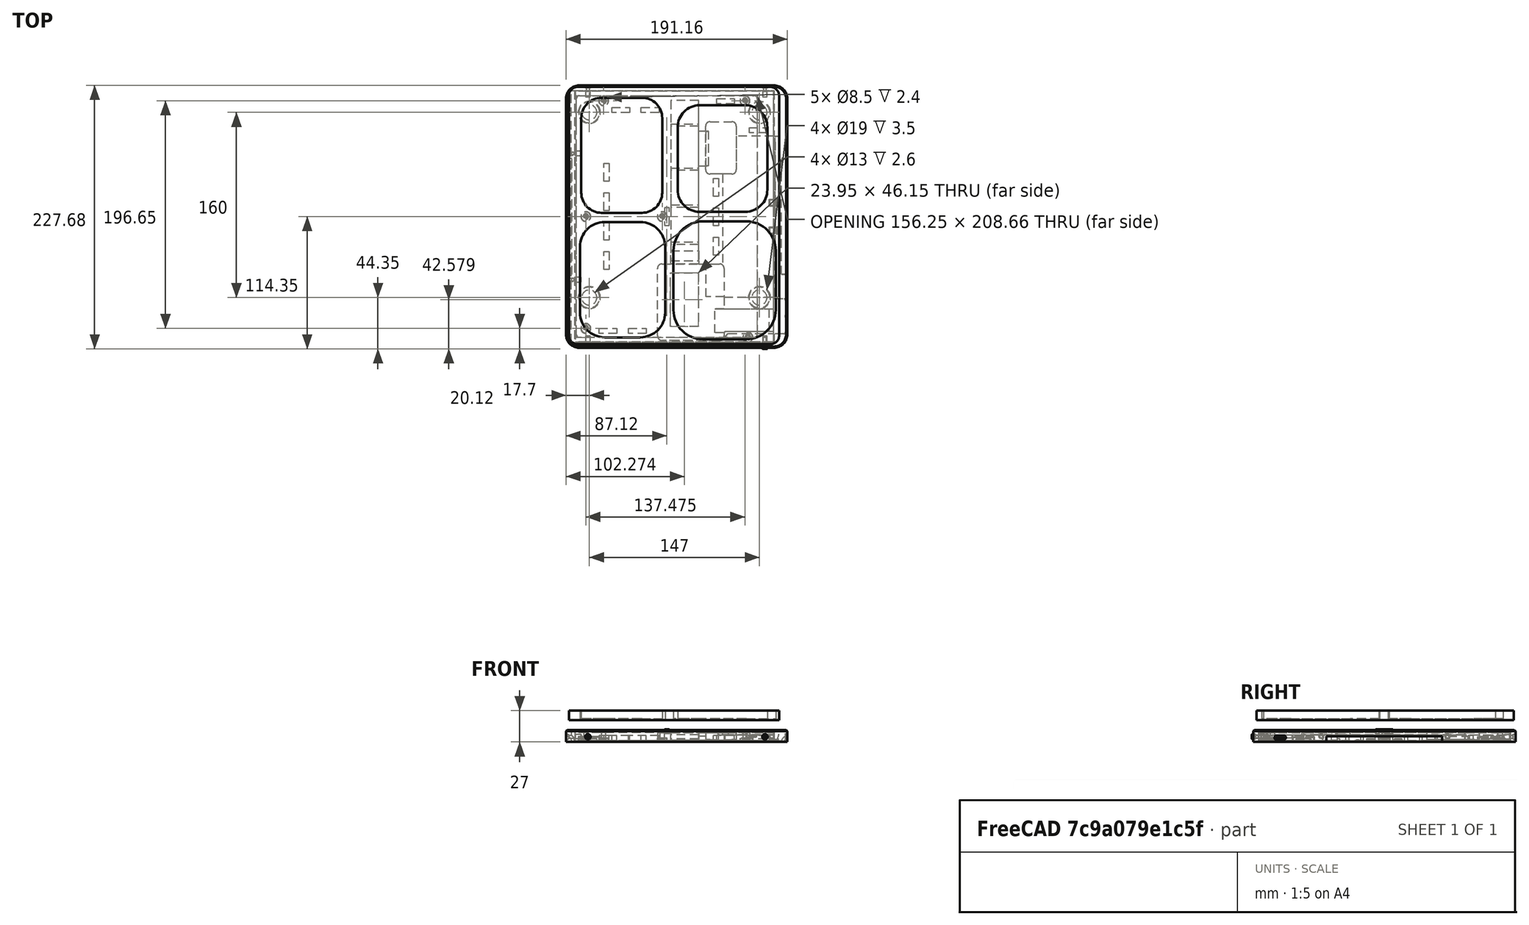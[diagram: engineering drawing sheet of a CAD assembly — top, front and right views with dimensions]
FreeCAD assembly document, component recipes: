
FREECAD ASSEMBLY — COMPONENT RECIPES ("freezer-display-assembly")

This assembly document has 5 components, labeled P0..P4 below (a component is one placed body or linked part). 5 of them carry a construction recipe — the FreeCAD feature program that regenerates the part from scratch, quoted from this document or its linked companion documents; the rest are supplied as boundary geometry only. No exploded tour is included for this assembly.
COMPONENT P0 — recipe-attached ("placeholder", modeled in this document).
Construction recipe (the document's own serialized feature program — sketch geometry with constraints, then the solid features built on it; lengths are millimeters unless a unit is written):

FEATURE [Sketcher::SketchObject] Sketch004
  AttachmentOffset = pos=(0,0,10) rot=(0,0,1;0rad)
  AttachmentSupport = -> [XY_Plane003]
  FullyConstrained = false
  MapMode = 5
  Placement = pos=(0,0,10) rot=(0,0,1;0rad)
  sketch-geometry (10):
    g0: ArcOfCircle CenterX=-77.1526 CenterY=104.437 CenterZ=0 NormalX=0 NormalY=0 NormalZ=1 AngleXU=0 Radius=7.5 StartAngle=1.5708 EndAngle=3.14159
    g1: LineSegment StartX=-77.1526 StartY=111.937 StartZ=0 EndX=89.4898 EndY=111.937 EndZ=0
    g2: ArcOfCircle CenterX=89.4898 CenterY=104.437 CenterZ=0 NormalX=0 NormalY=0 NormalZ=1 AngleXU=0 Radius=7.5 StartAngle=0 EndAngle=1.5708
    g3: LineSegment StartX=96.9898 StartY=104.437 StartZ=0 EndX=96.9898 EndY=-102.808 EndZ=0
    g4: ArcOfCircle CenterX=89.4898 CenterY=-102.808 CenterZ=0 NormalX=0 NormalY=0 NormalZ=1 AngleXU=0 Radius=7.5 StartAngle=4.71239 EndAngle=6.28319
    g5: LineSegment StartX=89.4898 StartY=-110.308 StartZ=0 EndX=-77.1526 EndY=-110.308 EndZ=0
    g6: ArcOfCircle CenterX=-77.1526 CenterY=-102.808 CenterZ=0 NormalX=0 NormalY=0 NormalZ=1 AngleXU=0 Radius=7.5 StartAngle=3.14159 EndAngle=4.71239
    g7: LineSegment StartX=-84.6526 StartY=-102.808 StartZ=0 EndX=-84.6526 EndY=104.437 EndZ=0
    g8: GeomPoint X=-84.6526 Y=111.937 Z=0
    g9: GeomPoint X=96.9898 Y=-110.308 Z=0
  constraints (20):
    c: Tangent(g0,g1) = 1.5708
    c: Tangent(g1,g2) = 1.5708
    c: Tangent(g2,g3) = 1.5708
    c: Tangent(g3,g4) = 1.5708
    c: Tangent(g4,g5) = 1.5708
    c: Tangent(g5,g6) = 1.5708
    c: Tangent(g6,g7) = 1.5708
    c: Tangent(g7,g0) = 1.5708
    c: Horizontal(g1)
    c: Horizontal(g5)
    c: Vertical(g3)
    c: Vertical(g7)
    c: Equal(g0,g2)
    c: Equal(g2,g4)
    c: Equal(g4,g6)
    c: PointOnObject(g8,g1)
    c: PointOnObject(g8,g7)
    c: PointOnObject(g9,g3)
    c: PointOnObject(g9,g5)
    c: Diameter(g4) = 15
FEATURE [PartDesign::Pad] Pad003
  Direction = (0,0,1)
  Length = 8
  Length2 = 10
  Profile = -> Sketch004
  ReferenceAxis = -> Sketch004 [N_Axis]
  Refine = true
  Suppressed = false
  Type = 0
FEATURE [Sketcher::SketchObject] Sketch005
  AttachmentSupport = -> [Pad003]
  FullyConstrained = false
  MapMode = 5
  Placement = pos=(0,0,18) rot=(0,0,1;0rad)
  sketch-geometry (40):
    g0: ArcOfCircle CenterX=-56.4829 CenterY=85.1627 CenterZ=0 NormalX=0 NormalY=0 NormalZ=1 AngleXU=0 Radius=17.496 StartAngle=1.5708 EndAngle=3.14159
    g1: LineSegment StartX=-56.4829 StartY=102.659 StartZ=0 EndX=-21.4911 EndY=102.659 EndZ=0
    g2: ArcOfCircle CenterX=-21.4911 CenterY=85.1627 CenterZ=0 NormalX=0 NormalY=0 NormalZ=1 AngleXU=0 Radius=17.496 StartAngle=1e-16 EndAngle=1.5708
    g3: LineSegment StartX=-3.99511 StartY=85.1627 StartZ=0 EndX=-3.99511 EndY=20.7193 EndZ=0
    g4: ArcOfCircle CenterX=-21.4911 CenterY=20.7193 CenterZ=0 NormalX=0 NormalY=0 NormalZ=1 AngleXU=0 Radius=17.496 StartAngle=4.71239 EndAngle=6.28319
    g5: LineSegment StartX=-21.4911 StartY=3.22331 StartZ=0 EndX=-56.4829 EndY=3.22331 EndZ=0
    g6: ArcOfCircle CenterX=-56.4829 CenterY=20.7193 CenterZ=0 NormalX=0 NormalY=0 NormalZ=1 AngleXU=0 Radius=17.496 StartAngle=3.14159 EndAngle=4.71239
    g7: LineSegment StartX=-73.9789 StartY=20.7193 StartZ=0 EndX=-73.9789 EndY=85.1627 EndZ=0
    g8: GeomPoint X=-73.9789 Y=102.659 Z=0
    g9: GeomPoint X=-3.99511 Y=3.22331 Z=0
    g10: ArcOfCircle CenterX=28.3724 CenterY=77.0631 CenterZ=0 NormalX=0 NormalY=0 NormalZ=1 AngleXU=0 Radius=19.05 StartAngle=1.5708 EndAngle=3.14159
    g11: LineSegment StartX=28.3724 StartY=96.1131 StartZ=0 EndX=67.8034 EndY=96.1131 EndZ=0
    g12: ArcOfCircle CenterX=67.8034 CenterY=77.0631 CenterZ=0 NormalX=0 NormalY=0 NormalZ=1 AngleXU=0 Radius=19.05 StartAngle=1e-16 EndAngle=1.5708
    g13: LineSegment StartX=86.8535 StartY=77.0631 StartZ=0 EndX=86.8535 EndY=23.1482 EndZ=0
    g14: ArcOfCircle CenterX=67.8034 CenterY=23.1482 CenterZ=0 NormalX=0 NormalY=0 NormalZ=1 AngleXU=0 Radius=19.05 StartAngle=4.71239 EndAngle=6.28319
    g15: LineSegment StartX=67.8034 StartY=4.09812 StartZ=0 EndX=28.3724 EndY=4.09812 EndZ=0
    g16: ArcOfCircle CenterX=28.3724 CenterY=23.1482 CenterZ=0 NormalX=0 NormalY=0 NormalZ=1 AngleXU=0 Radius=19.05 StartAngle=3.14159 EndAngle=4.71239
    g17: LineSegment StartX=9.32233 StartY=23.1482 StartZ=0 EndX=9.32233 EndY=77.0631 EndZ=0
    g18: GeomPoint X=9.32233 Y=96.1131 Z=0
    g19: GeomPoint X=86.8535 Y=4.09812 Z=0
    g20: ArcOfCircle CenterX=-53.6616 CenterY=-26.1553 CenterZ=0 NormalX=0 NormalY=0 NormalZ=1 AngleXU=0 Radius=21.4402 StartAngle=1.5708 EndAngle=3.14159
    g21: LineSegment StartX=-53.6616 StartY=-4.71507 StartZ=0 EndX=-22.8762 EndY=-4.71507 EndZ=0
    g22: ArcOfCircle CenterX=-22.8762 CenterY=-26.1553 CenterZ=0 NormalX=0 NormalY=0 NormalZ=1 AngleXU=0 Radius=21.4402 StartAngle=1e-16 EndAngle=1.5708
    g23: LineSegment StartX=-1.43594 StartY=-26.1553 StartZ=0 EndX=-1.43594 EndY=-82.893 EndZ=0
    g24: ArcOfCircle CenterX=-22.8762 CenterY=-82.893 CenterZ=0 NormalX=0 NormalY=0 NormalZ=1 AngleXU=0 Radius=21.4402 StartAngle=4.71239 EndAngle=6.28319
    g25: LineSegment StartX=-22.8762 StartY=-104.333 StartZ=0 EndX=-53.6616 EndY=-104.333 EndZ=0
    g26: ArcOfCircle CenterX=-53.6616 CenterY=-82.893 CenterZ=0 NormalX=0 NormalY=0 NormalZ=1 AngleXU=0 Radius=21.4402 StartAngle=3.14159 EndAngle=4.71239
    g27: LineSegment StartX=-75.1018 StartY=-82.893 StartZ=0 EndX=-75.1018 EndY=-26.1553 EndZ=0
    g28: GeomPoint X=-75.1018 Y=-4.71507 Z=0
    g29: GeomPoint X=-1.43594 Y=-104.333 Z=0
    g30: ArcOfCircle CenterX=30.9968 CenterY=-29.4358 CenterZ=0 NormalX=0 NormalY=0 NormalZ=1 AngleXU=0 Radius=25.2768 StartAngle=1.5708 EndAngle=3.14159
    g31: LineSegment StartX=30.9968 StartY=-4.15898 StartZ=0 EndX=68.8382 EndY=-4.15898 EndZ=0
    g32: ArcOfCircle CenterX=68.8382 CenterY=-29.4358 CenterZ=0 NormalX=0 NormalY=0 NormalZ=1 AngleXU=0 Radius=25.2768 StartAngle=2e-16 EndAngle=1.5708
    g33: LineSegment StartX=94.115 StartY=-29.4358 StartZ=0 EndX=94.115 EndY=-80.6908 EndZ=0
    g34: ArcOfCircle CenterX=68.8382 CenterY=-80.6908 CenterZ=0 NormalX=0 NormalY=0 NormalZ=1 AngleXU=0 Radius=25.2768 StartAngle=4.71239 EndAngle=6.28319
    g35: LineSegment StartX=68.8382 StartY=-105.968 StartZ=0 EndX=30.9968 EndY=-105.968 EndZ=0
    g36: ArcOfCircle CenterX=30.9968 CenterY=-80.6908 CenterZ=0 NormalX=0 NormalY=0 NormalZ=1 AngleXU=0 Radius=25.2768 StartAngle=3.14159 EndAngle=4.71239
    g37: LineSegment StartX=5.71998 StartY=-80.6908 StartZ=0 EndX=5.71998 EndY=-29.4358 EndZ=0
    g38: GeomPoint X=5.71998 Y=-4.15898 Z=0
    g39: GeomPoint X=94.115 Y=-105.968 Z=0
  constraints (76):
    c: Tangent(g0,g1) = 1.5708
    c: Tangent(g1,g2) = 1.5708
    c: Tangent(g2,g3) = 1.5708
    c: Tangent(g3,g4) = 1.5708
    c: Tangent(g4,g5) = 1.5708
    c: Tangent(g5,g6) = 1.5708
    c: Tangent(g6,g7) = 1.5708
    c: Tangent(g7,g0) = 1.5708
    c: Horizontal(g1)
    c: Horizontal(g5)
    c: Vertical(g3)
    c: Vertical(g7)
    c: Equal(g0,g2)
    c: Equal(g2,g4)
    c: Equal(g4,g6)
    c: PointOnObject(g8,g1)
    c: PointOnObject(g8,g7)
    c: PointOnObject(g9,g3)
    c: PointOnObject(g9,g5)
    c: Tangent(g10,g11) = 1.5708
    c: Tangent(g11,g12) = 1.5708
    c: Tangent(g12,g13) = 1.5708
    c: Tangent(g13,g14) = 1.5708
    c: Tangent(g14,g15) = 1.5708
    c: Tangent(g15,g16) = 1.5708
    c: Tangent(g16,g17) = 1.5708
    c: Tangent(g17,g10) = 1.5708
    c: Horizontal(g11)
    c: Horizontal(g15)
    c: Vertical(g13)
    c: Vertical(g17)
    c: Equal(g10,g12)
    c: Equal(g12,g14)
    c: Equal(g14,g16)
    c: PointOnObject(g18,g11)
    c: PointOnObject(g18,g17)
    c: PointOnObject(g19,g13)
    c: PointOnObject(g19,g15)
    c: Tangent(g20,g21) = 1.5708
    c: Tangent(g21,g22) = 1.5708
    c: Tangent(g22,g23) = 1.5708
    c: Tangent(g23,g24) = 1.5708
    c: Tangent(g24,g25) = 1.5708
    c: Tangent(g25,g26) = 1.5708
    c: Tangent(g26,g27) = 1.5708
    c: Tangent(g27,g20) = 1.5708
    c: Horizontal(g21)
    c: Horizontal(g25)
    c: Vertical(g23)
    c: Vertical(g27)
    c: Equal(g20,g22)
    c: Equal(g22,g24)
    c: Equal(g24,g26)
    c: PointOnObject(g28,g21)
    c: PointOnObject(g28,g27)
    c: PointOnObject(g29,g23)
    c: PointOnObject(g29,g25)
    c: Tangent(g30,g31) = 1.5708
    c: Tangent(g31,g32) = 1.5708
    c: Tangent(g32,g33) = 1.5708
    c: Tangent(g33,g34) = 1.5708
    c: Tangent(g34,g35) = 1.5708
    c: Tangent(g35,g36) = 1.5708
    c: Tangent(g36,g37) = 1.5708
    c: Tangent(g37,g30) = 1.5708
    c: Horizontal(g31)
    c: Horizontal(g35)
    c: Vertical(g33)
    c: Vertical(g37)
    c: Equal(g30,g32)
    c: Equal(g32,g34)
    c: Equal(g34,g36)
    c: PointOnObject(g38,g31)
    c: PointOnObject(g38,g37)
    c: PointOnObject(g39,g33)
    c: PointOnObject(g39,g35)
FEATURE [PartDesign::Pocket] Pocket
  BaseFeature = -> Pad003
  Direction = (0,0,-1)
  Length = 7
  Length2 = 5
  Profile = -> Sketch005
  ReferenceAxis = -> Sketch005 [N_Axis]
  Refine = true
  Suppressed = false
  Type = 0
FEATURE [PartDesign::Body] Body  label="placeholder"
  Group = -> [Sketch004,Pad003,Sketch005,Pocket]
  Origin = -> Origin003
  Tip = -> Pocket
COMPONENT P1 — recipe-attached ("SLS-frame", modeled in this document).
Construction recipe (the document's own serialized feature program — sketch geometry with constraints, then the solid features built on it; lengths are millimeters unless a unit is written):

FEATURE [Sketcher::SketchObject] Sketch006
  AttachmentSupport = -> [XY_Plane004]
  FullyConstrained = false
  MapMode = 5
  sketch-geometry (21):
    g0: ArcOfCircle CenterX=-75.625 CenterY=101.83 CenterZ=0 NormalX=0 NormalY=0 NormalZ=1 AngleXU=0 Radius=2.5 StartAngle=1.5708 EndAngle=3.14159
    g1: LineSegment StartX=-75.625 StartY=104.33 StartZ=0 EndX=75.625 EndY=104.33 EndZ=0
    g2: ArcOfCircle CenterX=75.625 CenterY=101.83 CenterZ=0 NormalX=0 NormalY=0 NormalZ=1 AngleXU=0 Radius=2.5 StartAngle=8e-16 EndAngle=1.5708
    g3: LineSegment StartX=78.125 StartY=101.83 StartZ=0 EndX=78.125 EndY=-101.83 EndZ=0
    g4: ArcOfCircle CenterX=75.625 CenterY=-101.83 CenterZ=0 NormalX=0 NormalY=0 NormalZ=1 AngleXU=0 Radius=2.5 StartAngle=4.71239 EndAngle=6.28319
    g5: LineSegment StartX=75.625 StartY=-104.33 StartZ=0 EndX=-75.625 EndY=-104.33 EndZ=0
    g6: ArcOfCircle CenterX=-75.625 CenterY=-101.83 CenterZ=0 NormalX=0 NormalY=0 NormalZ=1 AngleXU=0 Radius=2.5 StartAngle=3.14159 EndAngle=4.71239
    g7: LineSegment StartX=-78.125 StartY=-101.83 StartZ=0 EndX=-78.125 EndY=101.83 EndZ=0
    g8: GeomPoint X=-78.125 Y=104.33 Z=0
    g9: GeomPoint X=78.125 Y=-104.33 Z=0
    g10: ArcOfCircle CenterX=-75.625 CenterY=101.83 CenterZ=0 NormalX=0 NormalY=0 NormalZ=1 AngleXU=0 Radius=11.5 StartAngle=1.5708 EndAngle=3.14159
    g11: LineSegment StartX=-75.625 StartY=113.33 StartZ=0 EndX=92.5389 EndY=113.33 EndZ=0
    g12: ArcOfCircle CenterX=92.5389 CenterY=101.83 CenterZ=0 NormalX=0 NormalY=0 NormalZ=1 AngleXU=0 Radius=11.5 StartAngle=7e-16 EndAngle=1.5708
    g13: LineSegment StartX=104.039 StartY=101.83 StartZ=0 EndX=104.039 EndY=-101.83 EndZ=0
    g14: ArcOfCircle CenterX=92.5389 CenterY=-101.83 CenterZ=0 NormalX=0 NormalY=0 NormalZ=1 AngleXU=0 Radius=11.5 StartAngle=4.71239 EndAngle=6.28319
    g15: LineSegment StartX=92.5389 StartY=-113.33 StartZ=0 EndX=-75.625 EndY=-113.33 EndZ=0
    g16: ArcOfCircle CenterX=-75.625 CenterY=-101.83 CenterZ=0 NormalX=0 NormalY=0 NormalZ=1 AngleXU=0 Radius=11.5 StartAngle=3.14159 EndAngle=4.71239
    g17: LineSegment StartX=-87.125 StartY=-101.83 StartZ=0 EndX=-87.125 EndY=101.83 EndZ=0
    g18: GeomPoint X=-87.125 Y=113.33 Z=0
    g19: GeomPoint X=104.039 Y=-113.33 Z=0
    g20: LineSegment StartX=-83.7787 StartY=109.94 StartZ=0 EndX=-82.1303 EndY=108.314 EndZ=0
  constraints (45):
    c: Tangent(g0,g1) = 1.5708
    c: Tangent(g1,g2) = 1.5708
    c: Tangent(g2,g3) = 1.5708
    c: Tangent(g3,g4) = 1.5708
    c: Tangent(g4,g5) = 1.5708
    c: Tangent(g5,g6) = 1.5708
    c: Tangent(g6,g7) = 1.5708
    c: Tangent(g7,g0) = 1.5708
    c: Horizontal(g1)
    c: Horizontal(g5)
    c: Vertical(g3)
    c: Vertical(g7)
    c: Equal(g0,g2)
    c: Equal(g2,g4)
    c: PointOnObject(g8,g1)
    c: PointOnObject(g8,g7)
    c: PointOnObject(g9,g3)
    c: PointOnObject(g9,g5)
    c: Diameter(g4) = 5
    c: DistanceX(g0,g2) = 156.25
    c: Symmetric(g0,g4,g-1)
    c: DistanceY(g5,g0) = 208.66
    c: Tangent(g10,g11) = 1.5708
    c: Tangent(g11,g12) = 1.5708
    c: Tangent(g12,g13) = 1.5708
    c: Tangent(g13,g14) = 1.5708
    c: Tangent(g14,g15) = 1.5708
    c: Tangent(g15,g16) = 1.5708
    c: Tangent(g16,g17) = 1.5708
    c: Tangent(g17,g10) = 1.5708
    c: Horizontal(g11)
    c: Horizontal(g15)
    c: Vertical(g13)
    c: Equal(g10,g12)
    c: Equal(g12,g14)
    c: PointOnObject(g18,g11)
    c: PointOnObject(g18,g17)
    c: PointOnObject(g19,g13)
    c: PointOnObject(g19,g15)
    c: Diameter(g10) = 23
    c: Coincident(g10,g0)
    c: Symmetric(g10,g16,g-1)
    c: Coincident(g16,g6)
    c: PointOnObject(g20,g10)
    c: Distance(g20) = 2.31538
FEATURE [PartDesign::Pad] Pad004  label="front-opening-bulk-shape"
  Direction = (0,0,1)
  Length = 1.2
  Length2 = 9
  Profile = -> Sketch006
  ReferenceAxis = -> Sketch006 [N_Axis]
  Refine = true
  Suppressed = false
  Type = 4
FEATURE [Sketcher::SketchObject] Sketch007
  AttachmentSupport = -> [XY_Plane004]
  FullyConstrained = false
  MapMode = 5
  Placement = pos=(0,0,0) rot=(0,1,0;3.14159rad)
  expr: Constraints[8] = 174.4 + 1
  expr: Constraints[9] = 216.7 + 1
  sketch-geometry (4):
    g0: LineSegment StartX=82.6332 StartY=108.85 StartZ=0 EndX=-92.7668 EndY=108.85 EndZ=0
    g1: LineSegment StartX=-92.7668 StartY=108.85 StartZ=0 EndX=-92.7668 EndY=-108.85 EndZ=0
    g2: LineSegment StartX=-92.7668 StartY=-108.85 StartZ=0 EndX=82.6332 EndY=-108.85 EndZ=0
    g3: LineSegment StartX=82.6332 StartY=-108.85 StartZ=0 EndX=82.6332 EndY=108.85 EndZ=0
  constraints (10):
    c: Coincident(g0,g1)
    c: Coincident(g1,g2)
    c: Coincident(g2,g3)
    c: Coincident(g3,g0)
    c: Horizontal(g0)
    c: Horizontal(g2)
    c: Vertical(g1)
    c: Symmetric(g0,g2,g-1)
    c: DistanceX(g0,g0) = 175.4
    c: DistanceY(g3,g3) = 217.7
FEATURE [PartDesign::Pocket] Pocket001  label="dispaly-insertion-point"
  BaseFeature = -> Pad004
  Direction = (0,0,1)
  Length = 19
  Length2 = 5
  Profile = -> Sketch007
  ReferenceAxis = -> Sketch007 [N_Axis]
  Refine = true
  Reversed = true
  Suppressed = false
  Type = 0
FEATURE [Sketcher::SketchObject] Sketch008
  AttachmentSupport = -> [XZ_Plane004]
  ExternalGeometry = -> [Sketch006]
  FullyConstrained = false
  MapMode = 5
  Placement = pos=(0,0,0) rot=(1,0,0;1.5708rad)
  sketch-geometry (6):
    g0: Circle CenterX=-87.125 CenterY=-9 CenterZ=0 NormalX=0 NormalY=0 NormalZ=1 AngleXU=0 Radius=7.5
    g1: LineSegment StartX=-87.125 StartY=-9 StartZ=0 EndX=-87.125 EndY=0 EndZ=0
    g2: ArcOfCircle CenterX=-87.125 CenterY=-9 CenterZ=0 NormalX=0 NormalY=0 NormalZ=1 AngleXU=0 Radius=7.5 StartAngle=0 EndAngle=1.04963
    g3: LineSegment StartX=-87.125 StartY=-9 StartZ=0 EndX=-61.4654 EndY=-9 EndZ=0
    g4: LineSegment StartX=-79.625 StartY=-9 StartZ=0 EndX=-83.3908 EndY=-9 EndZ=0
    g5: LineSegment StartX=-83.3908 StartY=-2.49572 StartZ=0 EndX=-83.3908 EndY=-9 EndZ=0
  constraints (15):
    c: DistanceY(g0,g-1) = 9
    c: Diameter(g0) = 15
    c: Coincident(g1,g0)
    c: Coincident(g1,g-3)
    c: Vertical(g1)
    c: Coincident(g2,g0)
    c: PointOnObject(g2,g0)
    c: Coincident(g3,g2)
    c: Horizontal(g3)
    c: PointOnObject(g2,g3)
    c: Coincident(g4,g2)
    c: Vertical(g5)
    c: Coincident(g2,g5)
    c: Coincident(g4,g5)
    c: Horizontal(g4)
FEATURE [PartDesign::Pad] Pad005  label="handle-bulk"
  BaseFeature = -> Pocket001
  Direction = (0,-1,2e-16)
  Length = 220
  Length2 = 10
  Midplane = true
  Profile = -> Sketch008
  ReferenceAxis = -> Sketch008 [N_Axis]
  Refine = true
  Suppressed = false
  Type = 0
FEATURE [Sketcher::SketchObject] Sketch009
  AttachmentSupport = -> [XZ_Plane004]
  ExternalGeometry = -> [Sketch008,Sketch006]
  FullyConstrained = true
  MapMode = 5
  Placement = pos=(0,0,0) rot=(1,0,0;1.5708rad)
  sketch-geometry (8):
    g0: ArcOfCircle CenterX=-87.125 CenterY=-9 CenterZ=0 NormalX=0 NormalY=0 NormalZ=1 AngleXU=0 Radius=5 StartAngle=0 EndAngle=1.5708
    g1: LineSegment StartX=-82.125 StartY=-9 StartZ=0 EndX=-87.125 EndY=-9 EndZ=0
    g2: LineSegment StartX=-87.125 StartY=-9 StartZ=0 EndX=-87.125 EndY=-4 EndZ=0
    g3: LineSegment StartX=-79.625 StartY=-9 StartZ=0 EndX=104.039 EndY=-9 EndZ=0
    g4: ArcOfCircle CenterX=104.039 CenterY=-9 CenterZ=0 NormalX=0 NormalY=0 NormalZ=1 AngleXU=0 Radius=5 StartAngle=1.5708 EndAngle=3.14159
    g5: LineSegment StartX=104.039 StartY=-9 StartZ=0 EndX=104.039 EndY=0 EndZ=0
    g6: LineSegment StartX=99.0389 StartY=-9 StartZ=0 EndX=104.039 EndY=-9 EndZ=0
    g7: LineSegment StartX=104.039 StartY=-9 StartZ=0 EndX=104.039 EndY=-4 EndZ=0
  constraints (22):
    c: Coincident(g0,g-3)
    c: Coincident(g1,g0)
    c: Coincident(g1,g0)
    c: Horizontal(g1)
    c: Coincident(g2,g0)
    c: Coincident(g2,g0)
    c: Vertical(g2)
    c: DistanceX(g0,g-3) = 2.5
    c: DistanceY(g0,g0) = 5
    c: Coincident(g3,g-3)
    c: Horizontal(g3)
    c: Coincident(g4,g3)
    c: PointOnObject(g4,g3)
    c: Coincident(g5,g4)
    c: Coincident(g5,g-4)
    c: Vertical(g5)
    c: PointOnObject(g4,g5)
    c: Equal(g4,g0)
    c: Coincident(g6,g4)
    c: Coincident(g6,g4)
    c: Coincident(g7,g4)
    c: Coincident(g7,g4)
FEATURE [PartDesign::Pocket] Pocket002  label="handle-pocket"
  BaseFeature = -> Pad005
  Direction = (0,1,-2e-16)
  Length = 100
  Length2 = 5
  Midplane = true
  Profile = -> Sketch009
  ReferenceAxis = -> Sketch009 [N_Axis]
  Refine = true
  Suppressed = false
  Type = 0
FEATURE [Sketcher::SketchObject] Sketch010
  AttachmentSupport = -> [XZ_Plane004]
  ExternalGeometry = -> [Sketch007]
  FullyConstrained = true
  MapMode = 5
  Placement = pos=(0,0,0) rot=(1,0,0;1.5708rad)
  sketch-geometry (7):
    g0: LineSegment StartX=92.7668 StartY=-3.5e-15 StartZ=0 EndX=96.9668 EndY=-3.5e-15 EndZ=0
    g1: LineSegment StartX=96.9668 StartY=-3.5e-15 StartZ=0 EndX=96.9668 EndY=-8 EndZ=0
    g2: LineSegment StartX=96.9668 StartY=-8 StartZ=0 EndX=92.7668 EndY=-8 EndZ=0
    g3: LineSegment StartX=92.7668 StartY=-8 StartZ=0 EndX=92.7668 EndY=-3.6e-15 EndZ=0
    g4: ArcOfCircle CenterX=82.7106 CenterY=0 CenterZ=0 NormalX=0 NormalY=0 NormalZ=1 AngleXU=0 Radius=14.2562 StartAngle=5.59995 EndAngle=6.28319
    g5: LineSegment StartX=92.7668 StartY=-8 StartZ=0 EndX=92.7668 EndY=-9 EndZ=0
    g6: LineSegment StartX=92.7668 StartY=-9 StartZ=0 EndX=93.7668 EndY=-9 EndZ=0
  constraints (20):
    c: Coincident(g0,g1)
    c: Coincident(g1,g2)
    c: Coincident(g2,g3)
    c: Coincident(g3,g0)
    c: Horizontal(g0)
    c: Horizontal(g2)
    c: Vertical(g1)
    c: Vertical(g3)
    c: Coincident(g0,g-3)
    c: DistanceY(g1,g1) = 8
    c: DistanceX(g0,g0) = 4.2
    c: PointOnObject(g4,g-1)
    c: Coincident(g4,g0)
    c: Coincident(g2,g5)
    c: Vertical(g5)
    c: Coincident(g5,g6)
    c: Horizontal(g6)
    c: Equal(g6,g5)
    c: DistanceY(g5,g5) = 1
    c: Coincident(g4,g6)
FEATURE [PartDesign::Pocket] Pocket003  label="FPC-fold-cutout"
  BaseFeature = -> Pocket002
  Direction = (0,1,-2e-16)
  Length = 139
  Length2 = 5
  Midplane = true
  Profile = -> Sketch010
  ReferenceAxis = -> Sketch010 [N_Axis]
  Refine = true
  Suppressed = false
  Type = 0
FEATURE [PartDesign::Plane] DatumPlane  label="port-panel"
  Length = 154.963
  Placement = pos=(104.039,0,0) rot=(0.57735,0.57735,0.57735;2.0944rad)
  ResizeMode = 0
  Width = 66.6331
FEATURE [Sketcher::SketchObject] Sketch011
  AttachmentSupport = -> [DatumPlane]
  FullyConstrained = false
  MapMode = 5
  Placement = pos=(104.039,0,0) rot=(0.57735,0.57735,0.57735;2.0944rad)
  sketch-geometry (5):
    g0: ArcOfCircle CenterX=-93.0254 CenterY=-5.23827 CenterZ=0 NormalX=0 NormalY=0 NormalZ=1 AngleXU=0 Radius=1.9 StartAngle=1.5708 EndAngle=4.71239
    g1: ArcOfCircle CenterX=-86.9254 CenterY=-5.23827 CenterZ=0 NormalX=0 NormalY=0 NormalZ=1 AngleXU=0 Radius=1.9 StartAngle=4.71239 EndAngle=7.85398
    g2: LineSegment StartX=-93.0254 StartY=-7.13828 StartZ=0 EndX=-86.9254 EndY=-7.13828 EndZ=0
    g3: LineSegment StartX=-86.9254 StartY=-3.33827 StartZ=0 EndX=-93.0254 EndY=-3.33827 EndZ=0
    g4: Circle CenterX=-74.7278 CenterY=-6.01747 CenterZ=0 NormalX=0 NormalY=0 NormalZ=1 AngleXU=0 Radius=1.75
  constraints (9):
    c: Tangent(g0,g2) = -1.5708
    c: Tangent(g2,g1) = -1.5708
    c: Tangent(g1,g3) = -1.5708
    c: Tangent(g3,g0) = -1.5708
    c: Equal(g0,g1)
    c: Horizontal(g2)
    c: Diameter(g4) = 3.5
    c: Diameter(g1) = 3.8
    c: DistanceX(g0,g1) = 6.1
FEATURE [PartDesign::Pocket] Pocket004  label="ports"
  BaseFeature = -> Pocket003
  Direction = (-1,0,0)
  Length = 17
  Length2 = 5
  Profile = -> Sketch011
  ReferenceAxis = -> Sketch011 [N_Axis]
  Refine = true
  Suppressed = false
  Type = 0
FEATURE [PartDesign::Plane] DatumPlane001  label="bottom-surface"
  Length = 197.907
  Placement = pos=(0,0,-9) rot=(1,0,0;3.14159rad)
  ResizeMode = 0
  Width = 168.771
FEATURE [Sketcher::SketchObject] Sketch012
  AttachmentOffset = pos=(0,0,0.2) rot=(0,0,1;0rad)
  AttachmentSupport = -> [DatumPlane001]
  ExternalGeometry = -> [Sketch006]
  FullyConstrained = false
  MapMode = 5
  Placement = pos=(0,0,-9.2) rot=(1,0,0;3.14159rad)
  sketch-geometry (10):
    g0: ArcOfCircle CenterX=101.039 CenterY=99.7237 CenterZ=0 NormalX=0 NormalY=0 NormalZ=1 AngleXU=0 Radius=1.5 StartAngle=4e-16 EndAngle=1.5708
    g1: LineSegment StartX=102.539 StartY=99.7237 StartZ=0 EndX=102.539 EndY=72.4333 EndZ=0
    g2: ArcOfCircle CenterX=101.039 CenterY=72.4333 CenterZ=0 NormalX=0 NormalY=0 NormalZ=1 AngleXU=0 Radius=1.5 StartAngle=4.71239 EndAngle=6.28319
    g3: LineSegment StartX=101.039 StartY=70.9333 StartZ=0 EndX=49.8228 EndY=70.9333 EndZ=0
    g4: ArcOfCircle CenterX=49.8228 CenterY=72.4333 CenterZ=0 NormalX=0 NormalY=0 NormalZ=1 AngleXU=0 Radius=1.5 StartAngle=3.14159 EndAngle=4.71239
    g5: LineSegment StartX=48.3228 StartY=72.4333 StartZ=0 EndX=48.3228 EndY=99.7237 EndZ=0
    g6: ArcOfCircle CenterX=49.8228 CenterY=99.7237 CenterZ=0 NormalX=0 NormalY=0 NormalZ=1 AngleXU=0 Radius=1.5 StartAngle=1.5708 EndAngle=3.14159
    g7: LineSegment StartX=49.8228 StartY=101.224 StartZ=0 EndX=101.039 EndY=101.224 EndZ=0
    g8: GeomPoint X=102.539 Y=101.224 Z=0
    g9: GeomPoint X=48.3228 Y=70.9333 Z=0
  constraints (21):
    c: Tangent(g0,g1) = 1.5708
    c: Tangent(g1,g2) = 1.5708
    c: Tangent(g2,g3) = 1.5708
    c: Tangent(g3,g4) = 1.5708
    c: Tangent(g4,g5) = 1.5708
    c: Tangent(g5,g6) = 1.5708
    c: Tangent(g6,g7) = 1.5708
    c: Tangent(g7,g0) = 1.5708
    c: Horizontal(g3)
    c: Horizontal(g7)
    c: Vertical(g1)
    c: Vertical(g5)
    c: Equal(g0,g2)
    c: Equal(g2,g4)
    c: Equal(g4,g6)
    c: PointOnObject(g8,g1)
    c: PointOnObject(g8,g7)
    c: PointOnObject(g9,g3)
    c: PointOnObject(g9,g5)
    c: Diameter(g0) = 3
    c: DistanceX(g0,g-3) = 1.5
FEATURE [PartDesign::Pocket] Pocket005  label="PCB-cutout"
  BaseFeature = -> Pocket004
  Direction = (0,0,1)
  Length = 0
  Length2 = 5
  Profile = -> Sketch012
  ReferenceAxis = -> Sketch012 [N_Axis]
  Refine = true
  Suppressed = false
  Type = 3
  UpToFace = -> Pocket004 [Face2]
FEATURE [PartDesign::Plane] DatumPlane004  label="front-edge"
  Length = 185.768
  Placement = pos=(0,-113.33,0) rot=(1,0,0;1.5708rad)
  ResizeMode = 0
  Width = 68.3012
FEATURE [PartDesign::Plane] DatumPlane005  label="rear-edge"
  Length = 185.768
  Placement = pos=(0,113.33,0) rot=(0,0.707107,0.707107;3.14159rad)
  ResizeMode = 0
  Width = 68.3012
FEATURE [Sketcher::SketchObject] Sketch034
  AttachmentSupport = -> [DatumPlane004]
  FullyConstrained = true
  MapMode = 5
  Placement = pos=(0,-113.33,0) rot=(1,0,0;1.5708rad)
  sketch-geometry (3):
    g0: Circle CenterX=-68.2 CenterY=-4.5 CenterZ=0 NormalX=0 NormalY=0 NormalZ=1 AngleXU=0 Radius=2.3
    g1: Circle CenterX=84.8 CenterY=-4.5 CenterZ=0 NormalX=0 NormalY=0 NormalZ=1 AngleXU=0 Radius=2.3
    g2: LineSegment StartX=-68.2 StartY=-4.5 StartZ=0 EndX=84.8 EndY=-4.5 EndZ=0
  constraints (8):
    c: Coincident(g2,g0)
    c: Coincident(g2,g1)
    c: Horizontal(g2)
    c: Equal(g0,g1)
    c: DistanceY(g0,g-1) = 4.5
    c: Diameter(g0) = 4.6
    c: DistanceX(g-1,g1) = 84.8
    c: DistanceX(g0,g-1) = 68.2
FEATURE [PartDesign::Pocket] Pocket023  label="screwpoint-frame-front-clearance"
  BaseFeature = -> Pocket005
  Direction = (0,1,-2e-16)
  Length = 2
  Length2 = 5
  Profile = -> Sketch034
  ReferenceAxis = -> Sketch034 [N_Axis]
  Suppressed = false
  Type = 0
FEATURE [Sketcher::SketchObject] Sketch035
  AttachmentSupport = -> [DatumPlane004]
  ExternalGeometry = -> [Sketch034]
  FullyConstrained = true
  MapMode = 5
  Placement = pos=(0,-113.33,0) rot=(1,0,0;1.5708rad)
  sketch-geometry (2):
    g0: Circle CenterX=84.8 CenterY=-4.5 CenterZ=0 NormalX=0 NormalY=0 NormalZ=1 AngleXU=0 Radius=1.25
    g1: Circle CenterX=-68.2 CenterY=-4.5 CenterZ=0 NormalX=0 NormalY=0 NormalZ=1 AngleXU=0 Radius=1.25
  constraints (4):
    c: Coincident(g0,g-4)
    c: Coincident(g1,g-3)
    c: Equal(g1,g0)
    c: Diameter(g0) = 2.5
FEATURE [PartDesign::Pocket] Pocket024  label="screwpoint-frame-front-through"
  BaseFeature = -> Pocket023
  Direction = (0,1,-2e-16)
  Length = 16
  Length2 = 5
  Profile = -> Sketch035
  ReferenceAxis = -> Sketch035 [N_Axis]
  Suppressed = false
  Type = 0
FEATURE [Sketcher::SketchObject] Sketch037
  AttachmentSupport = -> [DatumPlane005]
  ExternalGeometry = -> [Sketch034]
  FullyConstrained = true
  MapMode = 5
  Placement = pos=(0,113.33,0) rot=(0,0.707107,0.707107;3.14159rad)
  sketch-geometry (2):
    g0: Circle CenterX=-84.8 CenterY=-4.5 CenterZ=0 NormalX=0 NormalY=0 NormalZ=1 AngleXU=0 Radius=2.3
    g1: Circle CenterX=68.2 CenterY=-4.5 CenterZ=0 NormalX=0 NormalY=0 NormalZ=1 AngleXU=0 Radius=2.3
  constraints (4):
    c: Coincident(g1,g-4)
    c: Coincident(g0,g-3)
    c: Equal(g0,g-3)
    c: Equal(g-4,g1)
FEATURE [PartDesign::Pocket] Pocket026  label="screwpoint-frame-rear-clearance"
  BaseFeature = -> Pocket024
  Direction = (0,-1,2e-16)
  Length = 2
  Length2 = 5
  Profile = -> Sketch037
  ReferenceAxis = -> Sketch037 [N_Axis]
  Suppressed = false
  Type = 0
FEATURE [Sketcher::SketchObject] Sketch038
  AttachmentSupport = -> [DatumPlane005]
  ExternalGeometry = -> [Sketch037]
  FullyConstrained = true
  MapMode = 5
  Placement = pos=(0,113.33,0) rot=(0,0.707107,0.707107;3.14159rad)
  sketch-geometry (2):
    g0: Circle CenterX=-84.8 CenterY=-4.5 CenterZ=0 NormalX=0 NormalY=0 NormalZ=1 AngleXU=0 Radius=1.3
    g1: Circle CenterX=68.2 CenterY=-4.5 CenterZ=0 NormalX=0 NormalY=0 NormalZ=1 AngleXU=0 Radius=1.3
  constraints (4):
    c: Equal(g0,g1)
    c: Coincident(g-4,g0)
    c: Diameter(g0) = 2.6
    c: Coincident(g1,g-3)
FEATURE [PartDesign::Pocket] Pocket027  label="screwpoint-frame-rear-through"
  BaseFeature = -> Pocket026
  Direction = (0,-1,2e-16)
  Length = 20
  Length2 = 5
  Profile = -> Sketch038
  ReferenceAxis = -> Sketch038 [N_Axis]
  Suppressed = false
  Type = 0
FEATURE [PartDesign::Chamfer] Chamfer002
  Angle = 45
  Base = -> Pocket027 [Edge100]
  BaseFeature = -> Pocket027
  ChamferType = 0
  FlipDirection = false
  Refine = true
  Size = 1
  Size2 = 1
  SupportTransform = false
  Suppressed = false
  UseAllEdges = false
FEATURE [PartDesign::Plane] DatumPlane007  label="grip-side"
  Length = 154.963
  Placement = pos=(-87.125,0,0) rot=(0.57735,-0.57735,-0.57735;2.0944rad)
  ResizeMode = 0
  Width = 66.6331
FEATURE [Sketcher::SketchObject] Sketch056
  AttachmentSupport = -> [DatumPlane007]
  FullyConstrained = true
  MapMode = 5
  Placement = pos=(-87.125,0,0) rot=(0.57735,-0.57735,-0.57735;2.0944rad)
  sketch-geometry (2):
    g0: Circle CenterX=-54.5 CenterY=-4.5 CenterZ=0 NormalX=0 NormalY=0 NormalZ=1 AngleXU=0 Radius=2.25
    g1: Circle CenterX=54.5 CenterY=-4.5 CenterZ=0 NormalX=0 NormalY=0 NormalZ=1 AngleXU=0 Radius=2.25
  constraints (5):
    c: Symmetric(g1,g0,g-2)
    c: Equal(g0,g1)
    c: Diameter(g1) = 4.5
    c: DistanceY(g0,g-1) = 4.5
    c: DistanceX(g0,g-1) = 54.5
FEATURE [PartDesign::Hole] Hole  label="screwpoint-frame-side"
  BaseFeature = -> Chamfer002
  CustomThreadClearance = 0
  Depth = 25
  DepthType = 0
  Diameter = 2.7
  DrillForDepth = false
  DrillPoint = 1
  DrillPointAngle = 118
  HoleCutCountersinkAngle = 90
  HoleCutCustomValues = false
  HoleCutDepth = 2
  HoleCutDiameter = 4.6
  HoleCutType = 1
  ModelThread = false
  Profile = -> Sketch056
  Refine = true
  Suppressed = false
  Tapered = false
  TaperedAngle = 90
  ThreadClass = 0
  ThreadDepth = 25
  ThreadDepthType = 0
  ThreadDirection = 0
  ThreadFit = 1
  ThreadSize = 8
  ThreadType = 1
  Threaded = false
  UseCustomThreadClearance = false
  expr: HoleCutDiameter = 4.6
FEATURE [Sketcher::SketchObject] Sketch058
  AttachmentOffset = pos=(0,0,12) rot=(0,0,1;0rad)
  AttachmentSupport = -> [XZ_Plane004]
  FullyConstrained = false
  MapMode = 5
  Placement = pos=(0,-12,2.7e-15) rot=(1,0,0;1.5708rad)
  sketch-geometry (4):
    g0: LineSegment StartX=92 StartY=-8 StartZ=0 EndX=96.3689 EndY=-8 EndZ=0
    g1: LineSegment StartX=96.3689 StartY=-8 StartZ=0 EndX=96.3689 EndY=-6.4 EndZ=0
    g2: LineSegment StartX=96.3689 StartY=-6.4 StartZ=0 EndX=92 EndY=-6.4 EndZ=0
    g3: LineSegment StartX=92 StartY=-6.4 StartZ=0 EndX=92 EndY=-8 EndZ=0
  constraints (10):
    c: Horizontal(g0)
    c: Coincident(g0,g1)
    c: Vertical(g1)
    c: Coincident(g1,g2)
    c: Horizontal(g2)
    c: Coincident(g2,g3)
    c: Coincident(g3,g0)
    c: Vertical(g3)
    c: DistanceY(g3,g3) = 1.6
    c: DistanceY(g0,g-1) = 8
FEATURE [PartDesign::Pocket] Pocket037  label="backpanel-latch-nook"
  BaseFeature = -> Hole
  Direction = (0,1,-2e-16)
  Length = 6
  Length2 = 5
  Midplane = true
  Profile = -> Sketch058
  ReferenceAxis = -> Sketch058 [N_Axis]
  Refine = true
  Suppressed = false
  Type = 0
FEATURE [PartDesign::Mirrored] Mirrored
  BaseFeature = -> Pocket037
  MirrorPlane = -> XZ_Plane004
  Originals = -> [Pocket037]
  Refine = true
  Suppressed = false
FEATURE [PartDesign::Body] Body001  label="SLS-frame"
  Group = -> [Sketch006,Pad004,Sketch007,Pocket001,Sketch008,Pad005,Sketch009,Pocket002,Sketch010,Pocket003,DatumPlane,Sketch011,Pocket004,DatumPlane001,Sketch012,Pocket005,Pocket023,Pocket024,Pocket026,Pocket027,Chamfer002,DatumPlane004,DatumPlane005,Sketch034,Sketch035,Sketch037,Sketch038,DatumPlane007,Sketch056,Hole,Sketch058,Pocket037,Mirrored]
  Origin = -> Origin004
  Tip = -> Mirrored
COMPONENT P2 — recipe-attached ("internal-frame", modeled in this document).
Construction recipe (the document's own serialized feature program — sketch geometry with constraints, then the solid features built on it; lengths are millimeters unless a unit is written):

FEATURE [Sketcher::SketchObject] Sketch017
  AttachmentOffset = pos=(0,0,8) rot=(0,0,1;0rad)
  AttachmentSupport = -> [XY_Plane006]
  FullyConstrained = true
  MapMode = 5
  Placement = pos=(0,0,-8) rot=(0,1,0;3.14159rad)
  sketch-geometry (5):
    g0: LineSegment StartX=-92.255 StartY=108.35 StartZ=0 EndX=79.145 EndY=108.35 EndZ=0
    g1: LineSegment StartX=79.145 StartY=108.35 StartZ=0 EndX=79.145 EndY=-108.35 EndZ=0
    g2: LineSegment StartX=79.145 StartY=-108.35 StartZ=0 EndX=-92.255 EndY=-108.35 EndZ=0
    g3: LineSegment StartX=-92.255 StartY=-108.35 StartZ=0 EndX=-92.255 EndY=108.35 EndZ=0
    g4: GeomPoint X=-79.145 Y=108.35 Z=0
  constraints (12):
    c: Coincident(g0,g1)
    c: Coincident(g1,g2)
    c: Coincident(g2,g3)
    c: Coincident(g3,g0)
    c: Horizontal(g0)
    c: Horizontal(g2)
    c: Vertical(g3)
    c: Symmetric(g0,g1,g-1)
    c: DistanceY(g1,g1) = 216.7
    c: Symmetric(g4,g0,g-2)
    c: DistanceX(g0,g-1) = 92.255
    c: DistanceX(g0,g0) = 171.4
FEATURE [PartDesign::Pad] Pad008  label="bulk"
  Direction = (0,0,-1)
  Length = 7
  Length2 = 10
  Profile = -> Sketch017
  ReferenceAxis = -> Sketch017 [N_Axis]
  Refine = true
  Reversed = true
  Suppressed = false
  Type = 0
FEATURE [PartDesign::Plane] DatumPlane002  label="back-side"
  Length = 209.945
  Placement = pos=(0,0,-8) rot=(1,0,0;3.14159rad)
  ResizeMode = 0
  Width = 255.245
FEATURE [PartDesign::Plane] DatumPlane003  label="dispaly-side"
  Length = 209.945
  Placement = pos=(0,0,-1) rot=(0,0,1;0rad)
  ResizeMode = 0
  Width = 255.245
FEATURE [Sketcher::SketchObject] Sketch020
  AttachmentSupport = -> [DatumPlane003]
  FullyConstrained = false
  MapMode = 5
  Placement = pos=(0,0,-1) rot=(0,0,1;0rad)
  sketch-geometry (4):
    g0: LineSegment StartX=109.341 StartY=69.5 StartZ=0 EndX=48.1742 EndY=69.5 EndZ=0
    g1: LineSegment StartX=48.1742 StartY=69.5 StartZ=0 EndX=48.1742 EndY=-69.5 EndZ=0
    g2: LineSegment StartX=48.1742 StartY=-69.5 StartZ=0 EndX=109.341 EndY=-69.5 EndZ=0
    g3: LineSegment StartX=109.341 StartY=-69.5 StartZ=0 EndX=109.341 EndY=69.5 EndZ=0
  constraints (9):
    c: Coincident(g1,g2)
    c: Coincident(g2,g3)
    c: Coincident(g3,g0)
    c: Horizontal(g0)
    c: Horizontal(g2)
    c: Vertical(g1)
    c: Coincident(g0,g1)
    c: Symmetric(g2,g0,g-1)
    c: DistanceY(g3,g3) = 139
FEATURE [PartDesign::Pocket] Pocket010  label="FPC-calbe-slot"
  BaseFeature = -> Pad008
  Direction = (0,0,-1)
  Length = 2
  Length2 = 5
  Profile = -> Sketch020
  ReferenceAxis = -> Sketch020 [N_Axis]
  Refine = true
  Suppressed = false
  Type = 0
FEATURE [Sketcher::SketchObject] Sketch021
  AttachmentSupport = -> [DatumPlane003]
  FullyConstrained = false
  MapMode = 5
  Placement = pos=(0,0,-1) rot=(0,0,1;0rad)
  sketch-geometry (10):
    g0: ArcOfCircle CenterX=56 CenterY=78.009 CenterZ=0 NormalX=0 NormalY=0 NormalZ=1 AngleXU=0 Radius=4 StartAngle=1.7e-15 EndAngle=1.5708
    g1: LineSegment StartX=60 StartY=78.009 StartZ=0 EndX=60 EndY=40.6525 EndZ=0
    g2: ArcOfCircle CenterX=56 CenterY=40.6525 CenterZ=0 NormalX=0 NormalY=0 NormalZ=1 AngleXU=0 Radius=4 StartAngle=4.71239 EndAngle=6.28319
    g3: LineSegment StartX=56 StartY=36.6525 StartZ=0 EndX=37.5 EndY=36.6525 EndZ=0
    g4: ArcOfCircle CenterX=37.5 CenterY=40.6525 CenterZ=0 NormalX=0 NormalY=0 NormalZ=1 AngleXU=0 Radius=4 StartAngle=3.14159 EndAngle=4.71239
    g5: LineSegment StartX=33.5 StartY=40.6525 StartZ=0 EndX=33.5 EndY=78.009 EndZ=0
    g6: ArcOfCircle CenterX=37.5 CenterY=78.009 CenterZ=0 NormalX=0 NormalY=0 NormalZ=1 AngleXU=0 Radius=4 StartAngle=1.5708 EndAngle=3.14159
    g7: LineSegment StartX=37.5 StartY=82.009 StartZ=0 EndX=56 EndY=82.009 EndZ=0
    g8: GeomPoint X=60 Y=82.009 Z=0
    g9: GeomPoint X=33.5 Y=36.6525 Z=0
  constraints (22):
    c: Tangent(g0,g1) = 1.5708
    c: Tangent(g1,g2) = 1.5708
    c: Tangent(g2,g3) = 1.5708
    c: Tangent(g3,g4) = 1.5708
    c: Tangent(g4,g5) = 1.5708
    c: Tangent(g5,g6) = 1.5708
    c: Tangent(g6,g7) = 1.5708
    c: Tangent(g7,g0) = 1.5708
    c: Horizontal(g3)
    c: Horizontal(g7)
    c: Vertical(g1)
    c: Vertical(g5)
    c: Equal(g0,g2)
    c: Equal(g2,g4)
    c: Equal(g4,g6)
    c: PointOnObject(g8,g1)
    c: PointOnObject(g8,g7)
    c: PointOnObject(g9,g3)
    c: PointOnObject(g9,g5)
    c: Diameter(g0) = 8
    c: DistanceX(g3,g3) = 18.5
    c: DistanceX(g-1,g2) = 56
FEATURE [PartDesign::Pocket] Pocket011  label="FPC-to-FFC-pocket"
  BaseFeature = -> Pocket010
  Direction = (0,0,-1)
  Length = 6
  Length2 = 5
  Profile = -> Sketch021
  ReferenceAxis = -> Sketch021 [N_Axis]
  Refine = true
  Suppressed = false
  Type = 0
FEATURE [Sketcher::SketchObject] Sketch022
  AttachmentSupport = -> [DatumPlane002]
  FullyConstrained = false
  MapMode = 5
  Placement = pos=(0,0,-8) rot=(1,0,0;3.14159rad)
  sketch-geometry (4):
    g0: LineSegment StartX=27.4009 StartY=-100.162 StartZ=0 EndX=3.40089 EndY=-100.162 EndZ=0
    g1: LineSegment StartX=3.40089 StartY=-100.162 StartZ=0 EndX=3.40089 EndY=38.2396 EndZ=0
    g2: LineSegment StartX=3.40089 StartY=38.2396 StartZ=0 EndX=27.4009 EndY=38.2396 EndZ=0
    g3: LineSegment StartX=27.4009 StartY=38.2396 StartZ=0 EndX=27.4009 EndY=-100.162 EndZ=0
  constraints (10):
    c: Coincident(g0,g1)
    c: Coincident(g1,g2)
    c: Coincident(g2,g3)
    c: Coincident(g3,g0)
    c: Horizontal(g0)
    c: Horizontal(g2)
    c: Vertical(g1)
    c: Vertical(g3)
    c: DistanceX(g2,g2) = 24
    c: DistanceX(g-1,g0) = 3.40089
FEATURE [PartDesign::Pocket] Pocket012  label="FFC-cable-slot"
  BaseFeature = -> Pocket011
  Direction = (0,0,1)
  Length = 5
  Length2 = 5
  Profile = -> Sketch022
  ReferenceAxis = -> Sketch022 [N_Axis]
  Refine = true
  Suppressed = false
  Type = 0
FEATURE [Sketcher::SketchObject] Sketch025
  AttachmentSupport = -> [DatumPlane003]
  FullyConstrained = false
  MapMode = 5
  Placement = pos=(0,0,-1) rot=(0,0,1;0rad)
  sketch-geometry (8):
    g0: LineSegment StartX=93.2468 StartY=-69.3047 StartZ=0 EndX=61.3879 EndY=-69.3047 EndZ=0
    g1: LineSegment StartX=61.3879 StartY=-69.3047 StartZ=0 EndX=55.0111 EndY=-64.2434 EndZ=0
    g2: LineSegment StartX=55.0111 StartY=-64.2434 StartZ=0 EndX=41.3305 EndY=-64.2434 EndZ=0
    g3: LineSegment StartX=41.3305 StartY=-64.2434 StartZ=0 EndX=41.3305 EndY=-102.943 EndZ=0
    g4: LineSegment StartX=48.6868 StartY=-105.844 StartZ=0 EndX=53.0779 EndY=-101.142 EndZ=0
    g5: LineSegment StartX=53.0779 StartY=-101.142 StartZ=0 EndX=93.2468 EndY=-101.142 EndZ=0
    g6: LineSegment StartX=93.2468 StartY=-101.142 StartZ=0 EndX=93.2468 EndY=-69.3047 EndZ=0
    g7: ArcOfCircle CenterX=45.5805 CenterY=-102.943 CenterZ=0 NormalX=0 NormalY=0 NormalZ=1 AngleXU=0 Radius=4.25 StartAngle=3.14159 EndAngle=5.532
  constraints (14):
    c: Horizontal(g0)
    c: Coincident(g0,g1)
    c: Coincident(g1,g2)
    c: Coincident(g2,g3)
    c: Vertical(g3)
    c: Coincident(g4,g5)
    c: Horizontal(g5)
    c: Coincident(g5,g6)
    c: Vertical(g6)
    c: Coincident(g0,g6)
    c: Horizontal(g2)
    c: Tangent(g7,g4) = -1.5708
    c: Tangent(g7,g3) = -1.5708
    c: Diameter(g7) = 8.5
FEATURE [PartDesign::Pocket] Pocket014  label="PCB-recess-1"
  BaseFeature = -> Pocket012
  Direction = (0,0,-1)
  Length = 1.9
  Length2 = 5
  Profile = -> Sketch025
  ReferenceAxis = -> Sketch025 [N_Axis]
  Refine = true
  Suppressed = false
  Type = 0
FEATURE [Sketcher::SketchObject] Sketch026
  AttachmentSupport = -> [DatumPlane003]
  FullyConstrained = false
  MapMode = 5
  Placement = pos=(0,0,-1) rot=(0,0,1;0rad)
  sketch-geometry (7):
    g0: LineSegment StartX=41.5727 StartY=-79.7249 StartZ=0 EndX=88.1006 EndY=-79.7249 EndZ=0
    g1: LineSegment StartX=88.1006 StartY=-79.7249 StartZ=0 EndX=88.1006 EndY=-99.5249 EndZ=0
    g2: LineSegment StartX=88.1006 StartY=-99.5249 StartZ=0 EndX=50.1347 EndY=-99.5249 EndZ=0
    g3: LineSegment StartX=41.5727 StartY=-99.4267 StartZ=0 EndX=41.5727 EndY=-79.7249 EndZ=0
    g4: LineSegment StartX=50.1347 StartY=-99.5249 StartZ=0 EndX=49.402 EndY=-100.487 EndZ=0
    g5: LineSegment StartX=49.402 StartY=-100.487 StartZ=0 EndX=41.5727 EndY=-100.487 EndZ=0
    g6: LineSegment StartX=41.5727 StartY=-100.487 StartZ=0 EndX=41.5727 EndY=-99.4267 EndZ=0
  constraints (15):
    c: Coincident(g0,g1)
    c: Coincident(g1,g2)
    c: Coincident(g3,g0)
    c: Horizontal(g0)
    c: Horizontal(g2)
    c: Vertical(g1)
    c: Vertical(g3)
    c: Coincident(g4,g5)
    c: Horizontal(g5)
    c: Coincident(g5,g6)
    c: Coincident(g6,g3)
    c: Vertical(g6)
    c: Coincident(g2,g4)
    c: DistanceX(g-1,g2) = 50.1347
    c: DistanceY(g1,g1) = 19.8
FEATURE [PartDesign::Pocket] Pocket015  label="PCB-recess-2"
  BaseFeature = -> Pocket014
  Direction = (0,0,-1)
  Length = 7
  Length2 = 5
  Profile = -> Sketch026
  ReferenceAxis = -> Sketch026 [N_Axis]
  Refine = true
  Suppressed = false
  Type = 0
FEATURE [Sketcher::SketchObject] Sketch027
  AttachmentSupport = -> [DatumPlane003]
  FullyConstrained = false
  MapMode = 5
  Placement = pos=(0,0,-1) rot=(0,0,1;0rad)
  sketch-geometry (10):
    g0: ArcOfCircle CenterX=-4.12153 CenterY=-44.9187 CenterZ=0 NormalX=0 NormalY=0 NormalZ=1 AngleXU=0 Radius=4 StartAngle=1.5708 EndAngle=3.14159
    g1: LineSegment StartX=-4.12153 StartY=-40.9187 StartZ=0 EndX=45.4999 EndY=-40.9187 EndZ=0
    g2: ArcOfCircle CenterX=45.4999 CenterY=-44.9187 CenterZ=0 NormalX=0 NormalY=0 NormalZ=1 AngleXU=0 Radius=4 StartAngle=7e-16 EndAngle=1.5708
    g3: LineSegment StartX=49.4999 StartY=-44.9187 StartZ=0 EndX=49.4999 EndY=-102.988 EndZ=0
    g4: ArcOfCircle CenterX=45.4999 CenterY=-102.988 CenterZ=0 NormalX=0 NormalY=0 NormalZ=1 AngleXU=0 Radius=4 StartAngle=4.71239 EndAngle=6.28319
    g5: LineSegment StartX=45.4999 StartY=-106.988 StartZ=0 EndX=-4.12153 EndY=-106.988 EndZ=0
    g6: ArcOfCircle CenterX=-4.12153 CenterY=-102.988 CenterZ=0 NormalX=0 NormalY=0 NormalZ=1 AngleXU=0 Radius=4 StartAngle=3.14159 EndAngle=4.71239
    g7: LineSegment StartX=-8.12153 StartY=-102.988 StartZ=0 EndX=-8.12153 EndY=-44.9187 EndZ=0
    g8: GeomPoint X=-8.12153 Y=-40.9187 Z=0
    g9: GeomPoint X=49.4999 Y=-106.988 Z=0
  constraints (20):
    c: Tangent(g0,g1) = 1.5708
    c: Tangent(g1,g2) = 1.5708
    c: Tangent(g2,g3) = 1.5708
    c: Tangent(g3,g4) = 1.5708
    c: Tangent(g4,g5) = 1.5708
    c: Tangent(g5,g6) = 1.5708
    c: Tangent(g6,g7) = 1.5708
    c: Tangent(g7,g0) = 1.5708
    c: Horizontal(g1)
    c: Horizontal(g5)
    c: Vertical(g3)
    c: Vertical(g7)
    c: Equal(g0,g2)
    c: Equal(g2,g4)
    c: Equal(g4,g6)
    c: PointOnObject(g8,g1)
    c: PointOnObject(g8,g7)
    c: PointOnObject(g9,g3)
    c: PointOnObject(g9,g5)
    c: Diameter(g4) = 8
FEATURE [PartDesign::Pocket] Pocket016  label="PCB-recess-3"
  BaseFeature = -> Pocket015
  Direction = (0,0,-1)
  Length = 6.5
  Length2 = 5
  Profile = -> Sketch027
  ReferenceAxis = -> Sketch027 [N_Axis]
  Refine = true
  Suppressed = false
  Type = 0
FEATURE [Sketcher::SketchObject] Sketch028
  AttachmentSupport = -> [DatumPlane003]
  ExternalGeometry = -> [Sketch022]
  FullyConstrained = false
  MapMode = 5
  Placement = pos=(0,0,-1) rot=(0,0,1;0rad)
  sketch-geometry (4):
    g0: LineSegment StartX=3.40089 StartY=-29.6561 StartZ=0 EndX=27.4009 EndY=-29.6561 EndZ=0
    g1: LineSegment StartX=27.4009 StartY=-29.6561 StartZ=0 EndX=27.4009 EndY=-41.6561 EndZ=0
    g2: LineSegment StartX=27.4009 StartY=-41.6561 StartZ=0 EndX=3.40089 EndY=-41.7974 EndZ=0
    g3: LineSegment StartX=3.40089 StartY=-41.7974 StartZ=0 EndX=3.40089 EndY=-29.6561 EndZ=0
  constraints (10):
    c: Coincident(g1,g2)
    c: Coincident(g2,g3)
    c: Vertical(g1)
    c: Vertical(g3)
    c: Coincident(g1,g0)
    c: Coincident(g3,g0)
    c: PointOnObject(g0,g-5)
    c: PointOnObject(g0,g-4)
    c: DistanceY(g1,g1) = 12
    c: Horizontal(g0)
FEATURE [PartDesign::Pocket] Pocket017  label="FFC-clearance-2"
  BaseFeature = -> Pocket016
  Direction = (0,0,-1)
  Length = 5.5
  Length2 = 5
  Profile = -> Sketch028
  ReferenceAxis = -> Sketch028 [N_Axis]
  Refine = true
  Suppressed = false
  Type = 0
FEATURE [Sketcher::SketchObject] Sketch029
  AttachmentSupport = -> [DatumPlane003]
  ExternalGeometry = -> [Sketch026]
  FullyConstrained = false
  MapMode = 5
  Placement = pos=(0,0,-1) rot=(0,0,1;0rad)
  sketch-geometry (4):
    g0: LineSegment StartX=88.1006 StartY=-79.7249 StartZ=0 EndX=94.3179 EndY=-79.7249 EndZ=0
    g1: LineSegment StartX=94.3179 StartY=-79.7249 StartZ=0 EndX=94.3179 EndY=-99.5249 EndZ=0
    g2: LineSegment StartX=94.3179 StartY=-99.5249 StartZ=0 EndX=88.1006 EndY=-99.5249 EndZ=0
    g3: LineSegment StartX=88.1006 StartY=-99.5249 StartZ=0 EndX=88.1006 EndY=-79.7249 EndZ=0
  constraints (9):
    c: Coincident(g0,g1)
    c: Coincident(g1,g2)
    c: Coincident(g2,g3)
    c: Coincident(g3,g0)
    c: Horizontal(g0)
    c: Horizontal(g2)
    c: Coincident(g0,g-3)
    c: Coincident(g2,g-4)
    c: Vertical(g1)
FEATURE [PartDesign::Pocket] Pocket018  label="PCB-recess-4"
  BaseFeature = -> Pocket017
  Direction = (0,0,-1)
  Length = 4.5
  Length2 = 5
  Profile = -> Sketch029
  ReferenceAxis = -> Sketch029 [N_Axis]
  Refine = true
  Suppressed = false
  Type = 0
FEATURE [Sketcher::SketchObject] Sketch031
  AttachmentSupport = -> [DatumPlane003]
  ExternalGeometry = -> [Sketch027]
  FullyConstrained = false
  MapMode = 5
  Placement = pos=(0,0,-1) rot=(0,0,1;0rad)
  sketch-geometry (9):
    g0: LineSegment StartX=3.18153 StartY=-48.6977 StartZ=0 EndX=27.1267 EndY=-48.6977 EndZ=0
    g1: LineSegment StartX=27.1267 StartY=-48.6977 StartZ=0 EndX=27.1267 EndY=-94.8437 EndZ=0
    g2: LineSegment StartX=27.1267 StartY=-94.8437 StartZ=0 EndX=3.18153 EndY=-94.8437 EndZ=0
    g3: LineSegment StartX=3.18153 StartY=-94.8437 StartZ=0 EndX=3.18153 EndY=-48.6977 EndZ=0
    g4: LineSegment StartX=33.974 StartY=-40.9187 StartZ=0 EndX=45.4999 EndY=-40.9187 EndZ=0
    g5: LineSegment StartX=49.4999 StartY=-44.9187 StartZ=0 EndX=49.4999 EndY=-69.3315 EndZ=0
    g6: LineSegment StartX=49.4999 StartY=-69.3315 StartZ=0 EndX=33.974 EndY=-69.3315 EndZ=0
    g7: LineSegment StartX=33.974 StartY=-69.3315 StartZ=0 EndX=33.974 EndY=-40.9187 EndZ=0
    g8: ArcOfCircle CenterX=45.4999 CenterY=-44.9187 CenterZ=0 NormalX=0 NormalY=0 NormalZ=1 AngleXU=0 Radius=4 StartAngle=2.8e-15 EndAngle=1.5708
  constraints (18):
    c: Coincident(g0,g1)
    c: Coincident(g1,g2)
    c: Coincident(g2,g3)
    c: Coincident(g3,g0)
    c: Horizontal(g0)
    c: Horizontal(g2)
    c: Vertical(g1)
    c: Vertical(g3)
    c: Coincident(g5,g6)
    c: Coincident(g6,g7)
    c: Coincident(g7,g4)
    c: Horizontal(g4)
    c: Horizontal(g6)
    c: Vertical(g5)
    c: Vertical(g7)
    c: Tangent(g4,g8) = 1.5708
    c: Coincident(g4,g-3)
    c: Coincident(g-3,g5)
FEATURE [PartDesign::Pocket] Pocket020  label="PCB-recess-5"
  BaseFeature = -> Pocket018
  Direction = (0,0,-1)
  Length = 25
  Length2 = 5
  Profile = -> Sketch031
  ReferenceAxis = -> Sketch031 [N_Axis]
  Refine = true
  Suppressed = false
  Type = 0
FEATURE [Sketcher::SketchObject] Sketch033
  AttachmentSupport = -> [DatumPlane002]
  FullyConstrained = false
  MapMode = 5
  Placement = pos=(0,0,-8) rot=(1,0,0;3.14159rad)
  sketch-geometry (4):
    g0: LineSegment StartX=23.6196 StartY=-43.7679 StartZ=0 EndX=35.9661 EndY=-43.7679 EndZ=0
    g1: LineSegment StartX=35.9661 StartY=-43.7679 StartZ=0 EndX=35.9661 EndY=-73.5802 EndZ=0
    g2: LineSegment StartX=35.9661 StartY=-73.5802 StartZ=0 EndX=23.6196 EndY=-73.5802 EndZ=0
    g3: LineSegment StartX=23.6196 StartY=-73.5802 StartZ=0 EndX=23.6196 EndY=-43.7679 EndZ=0
  constraints (8):
    c: Coincident(g0,g1)
    c: Coincident(g1,g2)
    c: Coincident(g2,g3)
    c: Coincident(g3,g0)
    c: Horizontal(g0)
    c: Horizontal(g2)
    c: Vertical(g1)
    c: Vertical(g3)
FEATURE [PartDesign::Pocket] Pocket022
  BaseFeature = -> Pocket020
  Direction = (0,0,1)
  Length = 4
  Length2 = 5
  Offset = 1
  Profile = -> Sketch033
  ReferenceAxis = -> Sketch033 [N_Axis]
  Suppressed = false
  Type = 0
FEATURE [Sketcher::SketchObject] Sketch036
  AttachmentSupport = -> [Pad008]
  FullyConstrained = true
  MapMode = 5
  Placement = pos=(0,-108.35,0) rot=(1,0,0;1.5708rad)
  expr: Constraints[6] = 3.9 + 3.2
  sketch-geometry (4):
    g0: Circle CenterX=-68.2 CenterY=-4.5 CenterZ=0 NormalX=0 NormalY=0 NormalZ=1 AngleXU=0 Radius=1.95
    g1: Circle CenterX=84.8 CenterY=-4.5 CenterZ=0 NormalX=0 NormalY=0 NormalZ=1 AngleXU=0 Radius=1.95
    g2: LineSegment StartX=84.8 StartY=-4.5 StartZ=0 EndX=-68.2 EndY=-4.5 EndZ=0
    g3: Circle CenterX=84.8 CenterY=-4.5 CenterZ=0 NormalX=0 NormalY=0 NormalZ=1 AngleXU=0 Radius=3.55
  constraints (10):
    c: Equal(g0,g1)
    c: Diameter(g1) = 3.9
    c: Coincident(g2,g1)
    c: Coincident(g2,g0)
    c: Horizontal(g2)
    c: Coincident(g3,g1)
    c: Diameter(g3) = 7.1
    c: DistanceY(g1,g-1) = 4.5
    c: DistanceX(g-1,g1) = 84.8
    c: DistanceX(g0,g-1) = 68.2
FEATURE [PartDesign::Pocket] Pocket025  label="front-heated-insert-m2.5-4mm"
  BaseFeature = -> Pocket022
  Direction = (0,1,-2e-16)
  Length = 5
  Length2 = 5
  Profile = -> Sketch036
  ReferenceAxis = -> Sketch036 [N_Axis]
  Suppressed = false
  Type = 0
FEATURE [Sketcher::SketchObject] Sketch039
  AttachmentSupport = -> [Pad008]
  ExternalGeometry = -> [Sketch036]
  FullyConstrained = true
  MapMode = 5
  Placement = pos=(0,108.35,0) rot=(0,0.707107,0.707107;3.14159rad)
  sketch-geometry (2):
    g0: Circle CenterX=-84.8 CenterY=-4.5 CenterZ=0 NormalX=0 NormalY=0 NormalZ=1 AngleXU=0 Radius=1.95
    g1: Circle CenterX=68.2 CenterY=-4.5 CenterZ=0 NormalX=0 NormalY=0 NormalZ=1 AngleXU=0 Radius=1.95
  constraints (4):
    c: Coincident(g1,g-4)
    c: Equal(g-4,g1)
    c: Coincident(g0,g-3)
    c: Equal(g-3,g0)
FEATURE [PartDesign::Pocket] Pocket028  label="rear-heated-insert-m2.5-4mm"
  BaseFeature = -> Pocket025
  Direction = (0,-1,2e-16)
  Length = 5
  Length2 = 5
  Profile = -> Sketch039
  ReferenceAxis = -> Sketch039 [N_Axis]
  Suppressed = false
  Type = 0
FEATURE [Sketcher::SketchObject] Sketch  label="extra-trusses-sketch"
  AttachmentSupport = -> [DatumPlane002]
  FullyConstrained = false
  MapMode = 5
  Placement = pos=(0,0,-8) rot=(1,0,0;3.14159rad)
  sketch-geometry (19):
    g0: LineSegment StartX=2.70492 StartY=24 StartZ=0 EndX=2.70492 EndY=22 EndZ=0
    g1: LineSegment StartX=2.70492 StartY=22 StartZ=0 EndX=30 EndY=22 EndZ=0
    g2: LineSegment StartX=30 StartY=22 StartZ=0 EndX=30 EndY=24 EndZ=0
    g3: LineSegment StartX=30 StartY=24 StartZ=0 EndX=2.70492 EndY=24 EndZ=0
    g4: LineSegment StartX=2.50997 StartY=-8 StartZ=0 EndX=2.50997 EndY=-10 EndZ=0
    g5: LineSegment StartX=2.50997 StartY=-10 StartZ=0 EndX=30 EndY=-10 EndZ=0
    g6: LineSegment StartX=30 StartY=-10 StartZ=0 EndX=30 EndY=-8 EndZ=0
    g7: LineSegment StartX=30 StartY=-8 StartZ=0 EndX=2.50997 EndY=-8 EndZ=0
    g8: LineSegment StartX=1.73116 StartY=-40 StartZ=0 EndX=1.73116 EndY=-42 EndZ=0
    g9: LineSegment StartX=1.73116 StartY=-42 StartZ=0 EndX=30 EndY=-42 EndZ=0
    g10: LineSegment StartX=30 StartY=-42 StartZ=0 EndX=30 EndY=-40 EndZ=0
    g11: LineSegment StartX=30 StartY=-40 StartZ=0 EndX=1.73116 EndY=-40 EndZ=0
    g12: LineSegment StartX=2.94796 StartY=-78 StartZ=0 EndX=2.94796 EndY=-80 EndZ=0
    g13: LineSegment StartX=2.94796 StartY=-80 StartZ=0 EndX=30 EndY=-80 EndZ=0
    g14: LineSegment StartX=30 StartY=-80 StartZ=0 EndX=30 EndY=-78 EndZ=0
    g15: LineSegment StartX=30 StartY=-78 StartZ=0 EndX=2.94796 EndY=-78 EndZ=0
    g16: LineSegment StartX=30 StartY=22 StartZ=0 EndX=30 EndY=-8 EndZ=0
    g17: LineSegment StartX=30 StartY=-10 StartZ=0 EndX=30 EndY=-40 EndZ=0
    g18: LineSegment StartX=30 StartY=-42 StartZ=0 EndX=30 EndY=-78 EndZ=0
  constraints (47):
    c: Coincident(g0,g1)
    c: Coincident(g1,g2)
    c: Coincident(g2,g3)
    c: Coincident(g3,g0)
    c: Vertical(g0)
    c: Vertical(g2)
    c: Horizontal(g1)
    c: Horizontal(g3)
    c: Coincident(g4,g5)
    c: Coincident(g5,g6)
    c: Coincident(g6,g7)
    c: Coincident(g7,g4)
    c: Vertical(g4)
    c: Vertical(g6)
    c: Horizontal(g5)
    c: Horizontal(g7)
    c: Coincident(g8,g9)
    c: Coincident(g9,g10)
    c: Coincident(g10,g11)
    c: Coincident(g11,g8)
    c: Vertical(g8)
    c: Vertical(g10)
    c: Horizontal(g9)
    c: Horizontal(g11)
    c: Coincident(g12,g13)
    c: Coincident(g13,g14)
    c: Coincident(g14,g15)
    c: Coincident(g15,g12)
    c: Vertical(g12)
    c: Vertical(g14)
    c: Horizontal(g13)
    c: Horizontal(g15)
    c: Equal(g14,g10)
    c: Equal(g10,g6)
    c: Equal(g6,g2)
    c: DistanceY(g2,g2) = 2
    c: Coincident(g1,g16)
    c: Coincident(g16,g6)
    c: Vertical(g16)
    c: Coincident(g5,g17)
    c: Coincident(g17,g10)
    c: Vertical(g17)
    c: Coincident(g9,g18)
    c: Coincident(g18,g14)
    c: Vertical(g18)
    c: Equal(g17,g16)
    c: DistanceY(g-1,g2) = 24
FEATURE [PartDesign::Pad] Pad  label="cable-guide-bars"
  BaseFeature = -> Pocket028
  Direction = (0,0,-1)
  Length = 1
  Length2 = 10
  Profile = -> Sketch
  ReferenceAxis = -> Sketch [N_Axis]
  Refine = true
  Reversed = true
  Suppressed = false
  Type = 0
FEATURE [Sketcher::SketchObject] Sketch045  label="bumpon locations"
  AttachmentSupport = -> [DatumPlane002]
  FullyConstrained = true
  MapMode = 5
  Placement = pos=(0,0,-8) rot=(1,0,0;3.14159rad)
  sketch-geometry (8):
    g0: Circle CenterX=-67 CenterY=70 CenterZ=0 NormalX=0 NormalY=0 NormalZ=1 AngleXU=0 Radius=6.35
    g1: Circle CenterX=80 CenterY=70 CenterZ=0 NormalX=0 NormalY=0 NormalZ=1 AngleXU=0 Radius=6.35
    g2: Circle CenterX=80 CenterY=-90 CenterZ=0 NormalX=0 NormalY=0 NormalZ=1 AngleXU=0 Radius=6.35
    g3: Circle CenterX=-67 CenterY=-90 CenterZ=0 NormalX=0 NormalY=0 NormalZ=1 AngleXU=0 Radius=6.35
    g4: LineSegment StartX=-67 StartY=70 StartZ=0 EndX=-67 EndY=-90 EndZ=0
    g5: LineSegment StartX=-67 StartY=-90 StartZ=0 EndX=80 EndY=-90 EndZ=0
    g6: LineSegment StartX=80 StartY=-90 StartZ=0 EndX=80 EndY=70 EndZ=0
    g7: LineSegment StartX=80 StartY=70 StartZ=0 EndX=-67 EndY=70 EndZ=0
  constraints (20):
    c: Equal(g1,g2)
    c: Equal(g2,g3)
    c: Diameter(g0) = 12.7
    c: Coincident(g4,g5)
    c: Coincident(g5,g6)
    c: Coincident(g6,g7)
    c: Coincident(g7,g4)
    c: Vertical(g4)
    c: Vertical(g6)
    c: Horizontal(g5)
    c: Horizontal(g7)
    c: Coincident(g4,g0)
    c: Coincident(g5,g2)
    c: Coincident(g1,g6)
    c: Coincident(g3,g4)
    c: DistanceY(g-1,g1) = 70
    c: Equal(g0,g1)
    c: DistanceX(g0,g-1) = 67
    c: DistanceX(g-1,g1) = 80
    c: DistanceY(g2,g-1) = 90
FEATURE [Sketcher::SketchObject] Sketch048  label="M2.5-screw-locations"
  AttachmentSupport = -> [DatumPlane002]
  FullyConstrained = false
  MapMode = 5
  Placement = pos=(0,0,-8) rot=(1,0,0;3.14159rad)
  sketch-geometry (9):
    g0: Circle CenterX=-70 CenterY=0 CenterZ=0 NormalX=0 NormalY=0 NormalZ=1 AngleXU=0 Radius=1.95
    g1: Circle CenterX=-70 CenterY=96.6497 CenterZ=0 NormalX=0 NormalY=0 NormalZ=1 AngleXU=0 Radius=1.95
    g2: Circle CenterX=67.4746 CenterY=-100 CenterZ=0 NormalX=0 NormalY=0 NormalZ=1 AngleXU=0 Radius=1.95
    g3: Circle CenterX=-54.6125 CenterY=-100 CenterZ=0 NormalX=0 NormalY=0 NormalZ=1 AngleXU=0 Radius=1.95
    g4: Circle CenterX=70 CenterY=104.171 CenterZ=0 NormalX=0 NormalY=0 NormalZ=1 AngleXU=0 Radius=1.95
    g5: LineSegment StartX=-70 StartY=96.6497 StartZ=0 EndX=-70 EndY=0 EndZ=0
    g6: LineSegment StartX=-54.6125 StartY=-100 StartZ=0 EndX=67.4746 EndY=-100 EndZ=0
    g7: Circle CenterX=-4 CenterY=0 CenterZ=0 NormalX=0 NormalY=0 NormalZ=1 AngleXU=0 Radius=1.95
    g8: Circle CenterX=-4 CenterY=0 CenterZ=0 NormalX=0 NormalY=0 NormalZ=1 AngleXU=0 Radius=3.5
  constraints (15):
    c: PointOnObject(g0,g-1)
    c: Equal(g0,g1)
    c: Equal(g1,g2)
    c: Equal(g2,g3)
    c: Coincident(g5,g1)
    c: Coincident(g5,g0)
    c: Vertical(g5)
    c: Coincident(g6,g3)
    c: Coincident(g6,g2)
    c: Horizontal(g6)
    c: PointOnObject(g7,g-1)
    c: Equal(g0,g7)
    c: Coincident(g8,g7)
    c: Diameter(g8) = 7
    c: Equal(g4,g1)
FEATURE [Sketcher::SketchObject] Sketch049
  AttachmentSupport = -> [DatumPlane002]
  ExternalGeometry = -> [Sketch045]
  FullyConstrained = true
  MapMode = 5
  Placement = pos=(0,0,-8) rot=(1,0,0;3.14159rad)
  sketch-geometry (4):
    g0: Circle CenterX=-67 CenterY=-90 CenterZ=0 NormalX=0 NormalY=0 NormalZ=1 AngleXU=0 Radius=9.5
    g1: Circle CenterX=80 CenterY=-90 CenterZ=0 NormalX=0 NormalY=0 NormalZ=1 AngleXU=0 Radius=9.5
    g2: Circle CenterX=80 CenterY=70 CenterZ=0 NormalX=0 NormalY=0 NormalZ=1 AngleXU=0 Radius=9.5
    g3: Circle CenterX=-67 CenterY=70 CenterZ=0 NormalX=0 NormalY=0 NormalZ=1 AngleXU=0 Radius=9.5
  constraints (8):
    c: Coincident(g0,g-6)
    c: Coincident(g1,g-5)
    c: Coincident(g2,g-4)
    c: Coincident(g3,g-3)
    c: Equal(g0,g1)
    c: Equal(g1,g2)
    c: Equal(g2,g3)
    c: Diameter(g2) = 19
FEATURE [PartDesign::Pocket] Pocket030  label="bumpon-pockets"
  BaseFeature = -> Pad
  Direction = (0,0,1)
  Length = 3.5
  Length2 = 5
  Profile = -> Sketch049
  ReferenceAxis = -> Sketch049 [N_Axis]
  Refine = true
  Suppressed = false
  Type = 0
FEATURE [Sketcher::SketchObject] Sketch053
  AttachmentSupport = -> [DatumPlane002]
  ExternalGeometry = -> [Sketch048]
  FullyConstrained = false
  MapMode = 5
  Placement = pos=(0,0,-8) rot=(1,0,0;3.14159rad)
  sketch-geometry (6):
    g0: Circle CenterX=-70 CenterY=0 CenterZ=0 NormalX=0 NormalY=0 NormalZ=1 AngleXU=0 Radius=4.25
    g1: Circle CenterX=-4 CenterY=0 CenterZ=0 NormalX=0 NormalY=0 NormalZ=1 AngleXU=0 Radius=4.25
    g2: Circle CenterX=70 CenterY=104.201 CenterZ=0 NormalX=0 NormalY=0 NormalZ=1 AngleXU=0 Radius=4.25
    g3: Circle CenterX=-70 CenterY=96.6497 CenterZ=0 NormalX=0 NormalY=0 NormalZ=1 AngleXU=0 Radius=4.25
    g4: Circle CenterX=67.4746 CenterY=-100 CenterZ=0 NormalX=0 NormalY=0 NormalZ=1 AngleXU=0 Radius=4.25
    g5: Circle CenterX=-54.6125 CenterY=-100 CenterZ=0 NormalX=0 NormalY=0 NormalZ=1 AngleXU=0 Radius=4.25
  constraints (6):
    c: Equal(g0,g1)
    c: Equal(g2,g3)
    c: Equal(g3,g4)
    c: Equal(g4,g5)
    c: Diameter(g4) = 8.5
    c: Equal(g4,g1)
FEATURE [PartDesign::Pocket] Pocket033  label="M2.5-inset"
  BaseFeature = -> Pocket030
  Direction = (0,0,1)
  Length = 2.4
  Length2 = 5
  Profile = -> Sketch053
  ReferenceAxis = -> Sketch053 [N_Axis]
  Refine = true
  Suppressed = false
  Type = 0
FEATURE [Sketcher::SketchObject] Sketch054
  AttachmentSupport = -> [DatumPlane002]
  ExternalGeometry = -> [Sketch048]
  FullyConstrained = true
  MapMode = 5
  Placement = pos=(0,0,-8) rot=(1,0,0;3.14159rad)
  sketch-geometry (6):
    g0: Circle CenterX=-70 CenterY=96.6497 CenterZ=0 NormalX=0 NormalY=0 NormalZ=1 AngleXU=0 Radius=1.95
    g1: Circle CenterX=70 CenterY=104.171 CenterZ=0 NormalX=0 NormalY=0 NormalZ=1 AngleXU=0 Radius=1.95
    g2: Circle CenterX=-4 CenterY=0 CenterZ=0 NormalX=0 NormalY=0 NormalZ=1 AngleXU=0 Radius=1.95
    g3: Circle CenterX=-70 CenterY=0 CenterZ=0 NormalX=0 NormalY=0 NormalZ=1 AngleXU=0 Radius=1.95
    g4: Circle CenterX=-54.6125 CenterY=-100 CenterZ=0 NormalX=0 NormalY=0 NormalZ=1 AngleXU=0 Radius=1.95
    g5: Circle CenterX=67.4746 CenterY=-100 CenterZ=0 NormalX=0 NormalY=0 NormalZ=1 AngleXU=0 Radius=1.95
  constraints (12):
    c: Coincident(g0,g-3)
    c: Coincident(g1,g-8)
    c: Coincident(g2,g-7)
    c: Coincident(g3,g-4)
    c: Coincident(g4,g-5)
    c: Coincident(g5,g-6)
    c: Equal(g0,g1)
    c: Equal(g1,g2)
    c: Equal(g2,g3)
    c: Equal(g3,g4)
    c: Equal(g4,g5)
    c: Diameter(g5) = 3.9
FEATURE [PartDesign::Pocket] Pocket034  label="M2.5-heated-inserts-slot"
  BaseFeature = -> Pocket033
  Direction = (0,0,1)
  Length = 15
  Length2 = 5
  Profile = -> Sketch054
  ReferenceAxis = -> Sketch054 [N_Axis]
  Refine = true
  Suppressed = false
  Type = 0
FEATURE [Sketcher::SketchObject] Sketch055
  AttachmentSupport = -> [DatumPlane002]
  FullyConstrained = false
  MapMode = 5
  Placement = pos=(0,0,-8) rot=(1,0,0;3.14159rad)
  sketch-geometry (61):
    g0: LineSegment StartX=-47.5358 StartY=-89.9675 StartZ=0 EndX=-47.5358 EndY=-94.3675 EndZ=0
    g1: LineSegment StartX=-47.5358 StartY=-94.3675 StartZ=0 EndX=-32.1358 EndY=-94.3675 EndZ=0
    g2: LineSegment StartX=-32.1358 StartY=-94.3675 StartZ=0 EndX=-32.1358 EndY=-89.9675 EndZ=0
    g3: LineSegment StartX=-32.1358 StartY=-89.9675 StartZ=0 EndX=-47.5358 EndY=-89.9675 EndZ=0
    g4: LineSegment StartX=-54.4 StartY=45.6414 StartZ=0 EndX=-54.4 EndY=30.2414 EndZ=0
    g5: LineSegment StartX=-54.4 StartY=30.2414 StartZ=0 EndX=-50 EndY=30.2414 EndZ=0
    g6: LineSegment StartX=-50 StartY=30.2414 StartZ=0 EndX=-50 EndY=45.6414 EndZ=0
    g7: LineSegment StartX=-50 StartY=45.6414 StartZ=0 EndX=-54.4 EndY=45.6414 EndZ=0
    g8: LineSegment StartX=-54.4 StartY=20.2414 StartZ=0 EndX=-54.4 EndY=4.84145 EndZ=0
    g9: LineSegment StartX=-54.4 StartY=4.84145 StartZ=0 EndX=-50 EndY=4.84145 EndZ=0
    g10: LineSegment StartX=-50 StartY=4.84145 StartZ=0 EndX=-50 EndY=20.2414 EndZ=0
    g11: LineSegment StartX=-50 StartY=20.2414 StartZ=0 EndX=-54.4 EndY=20.2414 EndZ=0
    g12: LineSegment StartX=-54.4 StartY=-5.15855 StartZ=0 EndX=-54.4 EndY=-20.5586 EndZ=0
    g13: LineSegment StartX=-54.4 StartY=-20.5586 StartZ=0 EndX=-50 EndY=-20.5586 EndZ=0
    g14: LineSegment StartX=-50 StartY=-20.5586 StartZ=0 EndX=-50 EndY=-5.15855 EndZ=0
    g15: LineSegment StartX=-50 StartY=-5.15855 StartZ=0 EndX=-54.4 EndY=-5.15855 EndZ=0
    g16: LineSegment StartX=-54.4 StartY=30.2414 StartZ=0 EndX=-54.4 EndY=20.2414 EndZ=0
    g17: LineSegment StartX=-54.4 StartY=20.2414 StartZ=0 EndX=-54.4 EndY=4.84145 EndZ=0
    g18: LineSegment StartX=-54.4 StartY=4.84145 StartZ=0 EndX=-54.4 EndY=-5.15855 EndZ=0
    g19: LineSegment StartX=-54.4 StartY=-30.5586 StartZ=0 EndX=-54.4 EndY=-45.9586 EndZ=0
    g20: LineSegment StartX=-54.4 StartY=-45.9586 StartZ=0 EndX=-50 EndY=-45.9586 EndZ=0
    g21: LineSegment StartX=-50 StartY=-45.9586 StartZ=0 EndX=-50 EndY=-30.5586 EndZ=0
    g22: LineSegment StartX=-50 StartY=-30.5586 StartZ=0 EndX=-54.4 EndY=-30.5586 EndZ=0
    g23: LineSegment StartX=-54.4 StartY=-20.5586 StartZ=0 EndX=-54.4 EndY=-30.5586 EndZ=0
    g24: LineSegment StartX=-22.1358 StartY=-89.9675 StartZ=0 EndX=-22.1358 EndY=-94.3675 EndZ=0
    g25: LineSegment StartX=-22.1358 StartY=-94.3675 StartZ=0 EndX=-6.73584 EndY=-94.3675 EndZ=0
    g26: LineSegment StartX=-6.73584 StartY=-94.3675 StartZ=0 EndX=-6.73584 EndY=-89.9675 EndZ=0
    g27: LineSegment StartX=-6.73584 StartY=-89.9675 StartZ=0 EndX=-22.1358 EndY=-89.9675 EndZ=0
    g28: LineSegment StartX=-32.1358 StartY=-94.3675 StartZ=0 EndX=-22.1358 EndY=-94.3675 EndZ=0
    g29: LineSegment StartX=-58.5514 StartY=101.033 StartZ=0 EndX=-58.5514 EndY=96.633 EndZ=0
    g30: LineSegment StartX=-58.5514 StartY=96.633 StartZ=0 EndX=-43.1514 EndY=96.633 EndZ=0
    g31: LineSegment StartX=-43.1514 StartY=96.633 StartZ=0 EndX=-43.1514 EndY=101.033 EndZ=0
    g32: LineSegment StartX=-43.1514 StartY=101.033 StartZ=0 EndX=-58.5514 EndY=101.033 EndZ=0
    g33: LineSegment StartX=-33.1514 StartY=101.033 StartZ=0 EndX=-33.1514 EndY=96.633 EndZ=0
    g34: LineSegment StartX=-33.1514 StartY=96.633 StartZ=0 EndX=-17.7514 EndY=96.633 EndZ=0
    g35: LineSegment StartX=-17.7514 StartY=96.633 StartZ=0 EndX=-17.7514 EndY=101.033 EndZ=0
    g36: LineSegment StartX=-17.7514 StartY=101.033 StartZ=0 EndX=-33.1514 EndY=101.033 EndZ=0
    g37: LineSegment StartX=-43.1514 StartY=101.033 StartZ=0 EndX=-33.1514 EndY=101.033 EndZ=0
    g38: LineSegment StartX=40.1887 StartY=33.3511 StartZ=0 EndX=40.1887 EndY=17.9511 EndZ=0
    g39: LineSegment StartX=40.1887 StartY=17.9511 StartZ=0 EndX=44.5887 EndY=17.9511 EndZ=0
    g40: LineSegment StartX=44.5887 StartY=17.9511 StartZ=0 EndX=44.5887 EndY=33.3511 EndZ=0
    g41: LineSegment StartX=44.5887 StartY=33.3511 StartZ=0 EndX=40.1887 EndY=33.3511 EndZ=0
    g42: LineSegment StartX=40.1887 StartY=7.95108 StartZ=0 EndX=40.1887 EndY=-7.44892 EndZ=0
    g43: LineSegment StartX=40.1887 StartY=-7.44892 StartZ=0 EndX=44.5887 EndY=-7.44892 EndZ=0
    g44: LineSegment StartX=44.5887 StartY=-7.44892 StartZ=0 EndX=44.5887 EndY=7.95108 EndZ=0
    g45: LineSegment StartX=44.5887 StartY=7.95108 StartZ=0 EndX=40.1887 EndY=7.95108 EndZ=0
    g46: LineSegment StartX=40.1887 StartY=-17.4489 StartZ=0 EndX=40.1887 EndY=-32.8489 EndZ=0
    g47: LineSegment StartX=40.1887 StartY=-32.8489 StartZ=0 EndX=44.5887 EndY=-32.8489 EndZ=0
    g48: LineSegment StartX=44.5887 StartY=-32.8489 StartZ=0 EndX=44.5887 EndY=-17.4489 EndZ=0
    g49: LineSegment StartX=44.5887 StartY=-17.4489 StartZ=0 EndX=40.1887 EndY=-17.4489 EndZ=0
    g50: LineSegment StartX=40.1887 StartY=17.9511 StartZ=0 EndX=40.1887 EndY=7.95108 EndZ=0
    g51: LineSegment StartX=40.1887 StartY=7.95108 StartZ=0 EndX=40.1887 EndY=-7.44892 EndZ=0
    g52: LineSegment StartX=40.1887 StartY=-7.44892 StartZ=0 EndX=40.1887 EndY=-17.4489 EndZ=0
    g53: LineSegment StartX=71.2518 StartY=-72.5021 StartZ=0 EndX=71.2518 EndY=-76.9021 EndZ=0
    g54: LineSegment StartX=71.2518 StartY=-76.9021 StartZ=0 EndX=86.6518 EndY=-76.9021 EndZ=0
    g55: LineSegment StartX=86.6518 StartY=-76.9021 StartZ=0 EndX=86.6518 EndY=-72.5021 EndZ=0
    g56: LineSegment StartX=86.6518 StartY=-72.5021 StartZ=0 EndX=71.2518 EndY=-72.5021 EndZ=0
    g57: LineSegment StartX=43.0828 StartY=-97.4155 StartZ=0 EndX=43.0828 EndY=-101.816 EndZ=0
    g58: LineSegment StartX=43.0828 StartY=-101.816 StartZ=0 EndX=58.4828 EndY=-101.816 EndZ=0
    g59: LineSegment StartX=58.4828 StartY=-101.816 StartZ=0 EndX=58.4828 EndY=-97.4155 EndZ=0
    g60: LineSegment StartX=58.4828 StartY=-97.4155 StartZ=0 EndX=43.0828 EndY=-97.4155 EndZ=0
  constraints (162):
    c: Coincident(g0,g1)
    c: Coincident(g1,g2)
    c: Coincident(g2,g3)
    c: Coincident(g3,g0)
    c: Vertical(g0)
    c: Vertical(g2)
    c: Horizontal(g1)
    c: Horizontal(g3)
    c: Coincident(g4,g5)
    c: Coincident(g5,g6)
    c: Coincident(g6,g7)
    c: Coincident(g7,g4)
    c: Vertical(g4)
    c: Vertical(g6)
    c: Horizontal(g5)
    c: Horizontal(g7)
    c: DistanceY(g4,g4) = 15.4
    c: DistanceX(g7,g7) = 4.4
    c: Coincident(g8,g9)
    c: Coincident(g9,g10)
    c: Coincident(g10,g11)
    c: Coincident(g11,g8)
    c: Vertical(g8)
    c: Vertical(g10)
    c: Horizontal(g9)
    c: Horizontal(g11)
    c: Coincident(g12,g13)
    c: Coincident(g13,g14)
    c: Coincident(g14,g15)
    c: Coincident(g15,g12)
    c: Vertical(g12)
    c: Vertical(g14)
    c: Horizontal(g13)
    c: Horizontal(g15)
    c: Equal(g8,g4)
    c: Equal(g4,g12)
    c: Equal(g7,g11)
    c: Equal(g11,g15)
    c: Coincident(g4,g16)
    c: Coincident(g16,g8)
    c: Coincident(g16,g17)
    c: Coincident(g17,g8)
    c: Coincident(g17,g18)
    c: Coincident(g18,g12)
    c: Vertical(g18)
    c: Vertical(g16)
    c: Equal(g16,g18)
    c: DistanceY(g16,g16) = 10
    c: Coincident(g19,g20)
    c: Coincident(g20,g21)
    c: Coincident(g21,g22)
    c: Coincident(g22,g19)
    c: Vertical(g19)
    c: Vertical(g21)
    c: Horizontal(g20)
    c: Horizontal(g22)
    c: Coincident(g12,g23)
    c: Coincident(g23,g19)
    c: Vertical(g23)
    c: Equal(g13,g22)
    c: Equal(g19,g12)
    c: Equal(g18,g23)
    c: DistanceX(g3,g3) = 15.4
    c: DistanceY(g2,g2) = 4.4
    c: Coincident(g24,g25)
    c: Coincident(g25,g26)
    c: Coincident(g26,g27)
    c: Coincident(g27,g24)
    c: Vertical(g24)
    c: Vertical(g26)
    c: Horizontal(g25)
    c: Horizontal(g27)
    c: Coincident(g1,g28)
    c: Coincident(g28,g24)
    c: Horizontal(g28)
    c: DistanceX(g28,g28) = 10
    c: Equal(g27,g3)
    c: Equal(g24,g2)
    c: Coincident(g29,g30)
    c: Coincident(g30,g31)
    c: Coincident(g31,g32)
    c: Coincident(g32,g29)
    c: Vertical(g29)
    c: Vertical(g31)
    c: Horizontal(g30)
    c: Horizontal(g32)
    c: Coincident(g33,g34)
    c: Coincident(g34,g35)
    c: Coincident(g35,g36)
    c: Coincident(g36,g33)
    c: Vertical(g33)
    c: Vertical(g35)
    c: Horizontal(g34)
    c: Horizontal(g36)
    c: Equal(g32,g36)
    c: Equal(g32,g3)
    c: Equal(g0,g29)
    c: Equal(g29,g33)
    c: Coincident(g31,g37)
    c: Coincident(g37,g33)
    c: Horizontal(g37)
    c: Equal(g37,g28)
    c: Coincident(g38,g39)
    c: Coincident(g39,g40)
    c: Coincident(g40,g41)
    c: Coincident(g41,g38)
    c: Vertical(g38)
    c: Vertical(g40)
    c: Horizontal(g39)
    c: Horizontal(g41)
    c: Coincident(g42,g43)
    c: Coincident(g43,g44)
    c: Coincident(g44,g45)
    c: Coincident(g45,g42)
    c: Vertical(g42)
    c: Vertical(g44)
    c: Horizontal(g43)
    c: Horizontal(g45)
    c: Equal(g38,g42)
    c: Equal(g42,g4)
    c: Equal(g41,g45)
    c: Equal(g45,g11)
    c: Coincident(g46,g47)
    c: Coincident(g47,g48)
    c: Coincident(g48,g49)
    c: Coincident(g49,g46)
    c: Vertical(g46)
    c: Vertical(g48)
    c: Horizontal(g47)
    c: Horizontal(g49)
    c: Equal(g46,g42)
    c: Equal(g49,g43)
    c: Coincident(g38,g50)
    c: Coincident(g50,g42)
    c: Coincident(g50,g51)
    c: Coincident(g51,g42)
    c: Coincident(g51,g52)
    c: Coincident(g52,g46)
    c: Vertical(g52)
    c: Vertical(g50)
    c: Equal(g52,g16)
    c: Equal(g50,g52)
    c: Coincident(g53,g54)
    c: Coincident(g54,g55)
    c: Coincident(g55,g56)
    c: Coincident(g56,g53)
    c: Vertical(g53)
    c: Vertical(g55)
    c: Horizontal(g54)
    c: Horizontal(g56)
    c: Equal(g56,g3)
    c: Equal(g53,g0)
    c: Coincident(g57,g58)
    c: Coincident(g58,g59)
    c: Coincident(g59,g60)
    c: Coincident(g60,g57)
    c: Vertical(g57)
    c: Vertical(g59)
    c: Horizontal(g58)
    c: Horizontal(g60)
    c: Equal(g60,g56)
    c: Equal(g53,g57)
FEATURE [PartDesign::Pocket] Pocket035  label="magnet-slots"
  BaseFeature = -> Pocket034
  Direction = (0,0,1)
  Length = 4.4
  Length2 = 5
  Profile = -> Sketch055
  ReferenceAxis = -> Sketch055 [N_Axis]
  Refine = true
  Suppressed = false
  Type = 0
FEATURE [PartDesign::Body] Body002  label="internal-frame"
  Group = -> [Sketch017,Pad008,DatumPlane002,DatumPlane003,Sketch020,Pocket010,Sketch021,Pocket011,Sketch022,Pocket012,Sketch025,Pocket014,Sketch026,Pocket015,Sketch027,Pocket016,Sketch028,Pocket017,Sketch029,Pocket018,Pocket020,Sketch031,Sketch033,Pocket022,Sketch036,Pocket025,Sketch039,Pocket028,Sketch,Pad,Sketch045,Sketch048,Sketch049,Pocket030,Sketch053,Pocket033,Sketch054,Pocket034,Sketch055,Pocket035,+5 more]
  Origin = -> Origin006
  Tip = -> Pocket038
COMPONENT P3 — recipe-attached ("Back-panel", modeled in this document).
Construction recipe (the document's own serialized feature program — sketch geometry with constraints, then the solid features built on it; lengths are millimeters unless a unit is written):

FEATURE [PartDesign::Plane] DatumPlane006  label="reference-plane"
  Length = 221.368
  Placement = pos=(0,0,-9) rot=(1,0,0;3.14159rad)
  ResizeMode = 0
  Width = 256.384
FEATURE [PartDesign::SubShapeBinder] Binder  label="PCB-cutout-shape"
  BindCopyOnChange = 0
  BindMode = 0
  ClaimChildren = false
  Context = -> Body003 [Binder.]
  Fuse = false
  MakeFace = true
  OffsetFill = false
  OffsetIntersection = false
  OffsetJoinType = 0
  OffsetOpenResult = false
  PartialLoad = false
  Refine = true
  Relative = true
  Support = -> [Body001[Pocket005.Sketch012.]]
  _Version = 2
FEATURE [PartDesign::SubShapeBinder] Binder001  label="internal-frame-bulk"
  BindCopyOnChange = 0
  BindMode = 0
  ClaimChildren = false
  Context = -> Body003 [Binder001.]
  Fuse = false
  MakeFace = true
  OffsetFill = false
  OffsetIntersection = false
  OffsetJoinType = 0
  OffsetOpenResult = false
  PartialLoad = false
  Refine = true
  Relative = true
  Support = -> [Body002[Pad008.Sketch017.]]
  _Version = 2
FEATURE [Sketcher::SketchObject] Sketch044
  AttachmentSupport = -> [DatumPlane006]
  ExternalGeometry = -> [Binder,Binder001]
  FullyConstrained = false
  MapMode = 5
  Placement = pos=(0,0,-9) rot=(1,0,0;3.14159rad)
  sketch-geometry (15):
    g0: LineSegment StartX=-79.145 StartY=108.35 StartZ=0 EndX=-79.145 EndY=-108.35 EndZ=0
    g1: LineSegment StartX=-79.145 StartY=-108.35 StartZ=0 EndX=92.255 EndY=-108.35 EndZ=0
    g2: LineSegment StartX=92.255 StartY=-108.35 StartZ=0 EndX=92.255 EndY=-69.2062 EndZ=0
    g3: LineSegment StartX=92.2465 StartY=70.9333 StartZ=0 EndX=101.039 EndY=70.9333 EndZ=0
    g4: ArcOfCircle CenterX=101.039 CenterY=72.4333 CenterZ=0 NormalX=0 NormalY=0 NormalZ=1 AngleXU=0 Radius=1.5 StartAngle=4.71239 EndAngle=6.28319
    g5: LineSegment StartX=102.539 StartY=72.4333 StartZ=0 EndX=102.539 EndY=99.7237 EndZ=0
    g6: ArcOfCircle CenterX=101.039 CenterY=99.7237 CenterZ=0 NormalX=0 NormalY=0 NormalZ=1 AngleXU=0 Radius=1.5 StartAngle=-4.4e-15 EndAngle=1.5708
    g7: LineSegment StartX=101.039 StartY=101.224 StartZ=0 EndX=92.2465 EndY=101.224 EndZ=0
    g8: LineSegment StartX=92.2465 StartY=101.224 StartZ=0 EndX=92.2465 EndY=108.35 EndZ=0
    g9: LineSegment StartX=92.2465 StartY=108.35 StartZ=0 EndX=-79.145 EndY=108.35 EndZ=0
    g10: LineSegment StartX=92.2465 StartY=101.224 StartZ=0 EndX=92.2465 EndY=70.9333 EndZ=0
    g11: LineSegment StartX=92.2465 StartY=69.2593 StartZ=0 EndX=93.5443 EndY=69.2593 EndZ=0
    g12: LineSegment StartX=93.5443 StartY=69.2593 StartZ=0 EndX=93.5443 EndY=-69.2062 EndZ=0
    g13: LineSegment StartX=93.5443 StartY=-69.2062 StartZ=0 EndX=92.255 EndY=-69.2062 EndZ=0
    g14: LineSegment StartX=92.2465 StartY=69.2593 StartZ=0 EndX=92.2465 EndY=70.9333 EndZ=0
  constraints (34):
    c: Vertical(g0)
    c: Coincident(g0,g1)
    c: Horizontal(g1)
    c: Coincident(g1,g2)
    c: Vertical(g2)
    c: Coincident(g14,g3)
    c: Tangent(g3,g4) = -1.5708
    c: Tangent(g4,g5) = -1.5708
    c: Tangent(g5,g6) = -1.5708
    c: Tangent(g6,g7) = -1.5708
    c: Coincident(g7,g8)
    c: Vertical(g8)
    c: Coincident(g8,g9)
    c: Coincident(g9,g0)
    c: Horizontal(g9)
    c: Vertical(g5)
    c: Horizontal(g7)
    c: Horizontal(g3)
    c: Coincident(g7,g10)
    c: Coincident(g10,g14)
    c: Vertical(g10)
    c: Coincident(g4,g-4)
    c: Coincident(g-3,g6)
    c: Equal(g-3,g6)
    c: Coincident(g1,g-6)
    c: Coincident(g0,g-5)
    c: Coincident(g11,g12)
    c: Vertical(g12)
    c: Coincident(g12,g13)
    c: Horizontal(g13)
    c: Horizontal(g11)
    c: Coincident(g2,g13)
    c: Coincident(g14,g11)
    c: Vertical(g14)
FEATURE [PartDesign::Pad] Pad010
  Direction = (0,0,-1)
  Length = 1
  Length2 = 10
  Placement = pos=(0,0,-9) rot=(1,0,0;3.14159rad)
  Profile = -> Sketch044
  ReferenceAxis = -> Sketch044 [N_Axis]
  Refine = true
  Reversed = true
  Suppressed = false
  Type = 0
FEATURE [PartDesign::SubShapeBinder] Binder002  label="bumpon-locations"
  BindCopyOnChange = 0
  BindMode = 0
  ClaimChildren = false
  Context = -> Body003 [Binder002.]
  Fuse = false
  MakeFace = true
  OffsetFill = false
  OffsetIntersection = false
  OffsetJoinType = 0
  OffsetOpenResult = false
  PartialLoad = false
  Refine = true
  Relative = true
  Support = -> [Body002[Sketch045.]]
  _Version = 2
FEATURE [Sketcher::SketchObject] Sketch046
  AttachmentSupport = -> [DatumPlane006]
  ExternalGeometry = -> [Binder002]
  FullyConstrained = false
  MapMode = 5
  Placement = pos=(0,0,-9) rot=(1,0,0;3.14159rad)
  sketch-geometry (4):
    g0: Circle CenterX=-67.0755 CenterY=70 CenterZ=0 NormalX=0 NormalY=0 NormalZ=1 AngleXU=0 Radius=9
    g1: Circle CenterX=80 CenterY=70 CenterZ=0 NormalX=0 NormalY=0 NormalZ=1 AngleXU=0 Radius=9
    g2: Circle CenterX=80 CenterY=-90 CenterZ=0 NormalX=0 NormalY=0 NormalZ=1 AngleXU=0 Radius=9
    g3: Circle CenterX=-67 CenterY=-90 CenterZ=0 NormalX=0 NormalY=0 NormalZ=1 AngleXU=0 Radius=9
  constraints (7):
    c: Coincident(g1,g-4)
    c: Coincident(g2,g-5)
    c: Coincident(g3,g-6)
    c: Equal(g3,g0)
    c: Equal(g0,g1)
    c: Equal(g1,g2)
    c: Diameter(g1) = 18
FEATURE [PartDesign::Pad] Pad011  label="bumpon-reinforcement"
  BaseFeature = -> Pad010
  Direction = (0,0,-1)
  Length = 4
  Length2 = 10
  Placement = pos=(0,0,-9) rot=(1,0,0;3.14159rad)
  Profile = -> Sketch046
  ReferenceAxis = -> Sketch046 [N_Axis]
  Refine = true
  Reversed = true
  Suppressed = false
  Type = 0
FEATURE [Sketcher::SketchObject] Sketch047
  AttachmentSupport = -> [DatumPlane006]
  ExternalGeometry = -> [Binder002]
  FullyConstrained = true
  MapMode = 5
  Placement = pos=(0,0,-9) rot=(1,0,0;3.14159rad)
  sketch-geometry (4):
    g0: Circle CenterX=-67 CenterY=70 CenterZ=0 NormalX=0 NormalY=0 NormalZ=1 AngleXU=0 Radius=6.5
    g1: Circle CenterX=80 CenterY=70 CenterZ=0 NormalX=0 NormalY=0 NormalZ=1 AngleXU=0 Radius=6.5
    g2: Circle CenterX=80 CenterY=-90 CenterZ=0 NormalX=0 NormalY=0 NormalZ=1 AngleXU=0 Radius=6.5
    g3: Circle CenterX=-67 CenterY=-90 CenterZ=0 NormalX=0 NormalY=0 NormalZ=1 AngleXU=0 Radius=6.5
  constraints (8):
    c: Coincident(g0,g-3)
    c: Tangent(g1,g-5) = -1.5708
    c: Coincident(g2,g-6)
    c: Coincident(g3,g-7)
    c: Equal(g3,g2)
    c: Equal(g2,g1)
    c: Equal(g1,g0)
    c: Diameter(g1) = 13
FEATURE [PartDesign::Pocket] Pocket029  label="bumpon-cutout"
  BaseFeature = -> Pad011
  Direction = (0,0,1)
  Length = 2.6
  Length2 = 5
  Placement = pos=(0,0,-9) rot=(1,0,0;3.14159rad)
  Profile = -> Sketch047
  ReferenceAxis = -> Sketch047 [N_Axis]
  Refine = true
  Suppressed = false
  Type = 0
FEATURE [PartDesign::SubShapeBinder] Binder003  label="M2.5-screws"
  BindCopyOnChange = 0
  BindMode = 0
  ClaimChildren = false
  Context = -> Body003 [Binder003.]
  Fuse = false
  MakeFace = true
  OffsetFill = false
  OffsetIntersection = false
  OffsetJoinType = 0
  OffsetOpenResult = false
  PartialLoad = false
  Refine = true
  Relative = true
  Support = -> [Body002[Sketch048.]]
  _Version = 2
FEATURE [Sketcher::SketchObject] Sketch050
  AttachmentSupport = -> [DatumPlane006]
  ExternalGeometry = -> [Binder003]
  FullyConstrained = false
  MapMode = 5
  Placement = pos=(0,0,-9) rot=(1,0,0;3.14159rad)
  sketch-geometry (6):
    g0: Circle CenterX=-70 CenterY=0 CenterZ=0 NormalX=0 NormalY=0 NormalZ=1 AngleXU=0 Radius=4
    g1: Circle CenterX=-70 CenterY=96.6497 CenterZ=0 NormalX=0 NormalY=0 NormalZ=1 AngleXU=0 Radius=4
    g2: Circle CenterX=-4 CenterY=0 CenterZ=0 NormalX=0 NormalY=0 NormalZ=1 AngleXU=0 Radius=4
    g3: Circle CenterX=67.4746 CenterY=-100 CenterZ=0 NormalX=0 NormalY=0 NormalZ=1 AngleXU=0 Radius=4
    g4: Circle CenterX=-54.6125 CenterY=-100 CenterZ=0 NormalX=0 NormalY=0 NormalZ=1 AngleXU=0 Radius=4
    g5: Circle CenterX=70 CenterY=104.126 CenterZ=0 NormalX=0 NormalY=0 NormalZ=1 AngleXU=0 Radius=4
  constraints (6):
    c: Diameter(g0) = 8
    c: Equal(g0,g1)
    c: Equal(g1,g2)
    c: Equal(g3,g4)
    c: Equal(g4,g5)
    c: Equal(g5,g0)
FEATURE [PartDesign::Pad] Pad012  label="M2.5-reinforcements"
  BaseFeature = -> Pocket029
  Direction = (0,0,-1)
  Length = 3
  Length2 = 10
  Placement = pos=(0,0,-9) rot=(1,0,0;3.14159rad)
  Profile = -> Sketch050
  ReferenceAxis = -> Sketch050 [N_Axis]
  Refine = true
  Reversed = true
  Suppressed = false
  Type = 0
FEATURE [Sketcher::SketchObject] Sketch051
  AttachmentSupport = -> [DatumPlane006]
  ExternalGeometry = -> [Binder003]
  FullyConstrained = false
  MapMode = 5
  Placement = pos=(0,0,-9) rot=(1,0,0;3.14159rad)
  sketch-geometry (6):
    g0: Circle CenterX=-70 CenterY=0 CenterZ=0 NormalX=0 NormalY=0 NormalZ=1 AngleXU=0 Radius=2.4
    g1: Circle CenterX=-4 CenterY=0 CenterZ=0 NormalX=0 NormalY=0 NormalZ=1 AngleXU=0 Radius=2.4
    g2: Circle CenterX=67.4746 CenterY=-100 CenterZ=0 NormalX=0 NormalY=0 NormalZ=1 AngleXU=0 Radius=2.4
    g3: Circle CenterX=-54.6125 CenterY=-100 CenterZ=0 NormalX=0 NormalY=0 NormalZ=1 AngleXU=0 Radius=2.4
    g4: Circle CenterX=-70 CenterY=96.6497 CenterZ=0 NormalX=0 NormalY=0 NormalZ=1 AngleXU=0 Radius=2.4
    g5: Circle CenterX=70 CenterY=104.186 CenterZ=0 NormalX=0 NormalY=0 NormalZ=1 AngleXU=0 Radius=2.4
  constraints (5):
    c: Diameter(g5) = 4.8
    c: Equal(g1,g2)
    c: Equal(g2,g3)
    c: Equal(g3,g4)
    c: Equal(g4,g5)
FEATURE [PartDesign::Pocket] Pocket031  label="M2.5-head-cutout"
  BaseFeature = -> Pad012
  Direction = (0,0,1)
  Length = 2
  Length2 = 5
  Placement = pos=(0,0,-9) rot=(1,0,0;3.14159rad)
  Profile = -> Sketch051
  ReferenceAxis = -> Sketch051 [N_Axis]
  Refine = true
  Suppressed = false
  Type = 0
FEATURE [Sketcher::SketchObject] Sketch052
  AttachmentSupport = -> [DatumPlane006]
  ExternalGeometry = -> [Binder003]
  FullyConstrained = false
  MapMode = 5
  Placement = pos=(0,0,-9) rot=(1,0,0;3.14159rad)
  sketch-geometry (6):
    g0: Circle CenterX=-54.6125 CenterY=-100 CenterZ=0 NormalX=0 NormalY=0 NormalZ=1 AngleXU=0 Radius=1.25
    g1: Circle CenterX=67.4746 CenterY=-100 CenterZ=0 NormalX=0 NormalY=0 NormalZ=1 AngleXU=0 Radius=1.25
    g2: Circle CenterX=-4 CenterY=0 CenterZ=0 NormalX=0 NormalY=0 NormalZ=1 AngleXU=0 Radius=1.25
    g3: Circle CenterX=-70 CenterY=0 CenterZ=0 NormalX=0 NormalY=0 NormalZ=1 AngleXU=0 Radius=1.25
    g4: Circle CenterX=70 CenterY=104.13 CenterZ=0 NormalX=0 NormalY=0 NormalZ=1 AngleXU=0 Radius=1.25
    g5: Circle CenterX=-70 CenterY=96.6497 CenterZ=0 NormalX=0 NormalY=0 NormalZ=1 AngleXU=0 Radius=1.25
  constraints (4):
    c: Equal(g0,g1)
    c: Equal(g2,g3)
    c: Equal(g3,g4)
    c: Equal(g4,g5)
FEATURE [PartDesign::Pocket] Pocket032  label="M2.5-shaft-cutout"
  BaseFeature = -> Pocket031
  Direction = (0,0,1)
  Length = 5
  Length2 = 5
  Placement = pos=(0,0,-9) rot=(1,0,0;3.14159rad)
  Profile = -> Sketch052
  ReferenceAxis = -> Sketch052 [N_Axis]
  Refine = true
  Suppressed = false
  Type = 0
FEATURE [PartDesign::CoordinateSystem] bumppon_A  label="bumppon-A"
  AttacherType = Attacher::AttachEngine3D
  AttachmentSupport = -> [Pocket032]
  MapMode = 45
  Placement = pos=(-54.6125,100,-7) rot=(0,0,1;0rad)
FEATURE [PartDesign::CoordinateSystem] bumppon_B  label="bumppon-B"
  AttacherType = Attacher::AttachEngine3D
  AttachmentSupport = -> [Pocket032]
  MapMode = 45
  Placement = pos=(80,90,-6.5) rot=(0,0,1;0rad)
FEATURE [PartDesign::CoordinateSystem] bumppon_C  label="bumppon-C"
  AttacherType = Attacher::AttachEngine3D
  AttachmentSupport = -> [Pocket029]
  MapMode = 45
  Placement = pos=(-67,90,-6.5) rot=(0,0,1;0rad)
FEATURE [PartDesign::CoordinateSystem] bumppon_D  label="bumppon-D"
  AttacherType = Attacher::AttachEngine3D
  AttachmentSupport = -> [Pocket029]
  MapMode = 45
  Placement = pos=(80,90,-6.5) rot=(0,0,1;0rad)
FEATURE [Sketcher::SketchObject] Sketch059
  AttachmentOffset = pos=(0,0,-1) rot=(0,0,1;0rad)
  AttachmentSupport = -> [DatumPlane006]
  FullyConstrained = false
  MapMode = 5
  Placement = pos=(0,0,-8) rot=(1,0,0;3.14159rad)
  sketch-geometry (10):
    g0: LineSegment StartX=89 StartY=14.5 StartZ=0 EndX=89 EndY=9.5 EndZ=0
    g1: LineSegment StartX=89 StartY=9.5 StartZ=0 EndX=96 EndY=9.5 EndZ=0
    g2: LineSegment StartX=96 StartY=9.5 StartZ=0 EndX=96 EndY=14.5 EndZ=0
    g3: LineSegment StartX=96 StartY=14.5 StartZ=0 EndX=89 EndY=14.5 EndZ=0
    g4: LineSegment StartX=89 StartY=-9.5 StartZ=0 EndX=89 EndY=-14.5 EndZ=0
    g5: LineSegment StartX=89 StartY=-14.5 StartZ=0 EndX=95.4116 EndY=-14.5 EndZ=0
    g6: LineSegment StartX=95.4116 StartY=-14.5 StartZ=0 EndX=95.4116 EndY=-9.5 EndZ=0
    g7: LineSegment StartX=95.4116 StartY=-9.5 StartZ=0 EndX=89 EndY=-9.5 EndZ=0
    g8: LineSegment StartX=89 StartY=14.5 StartZ=0 EndX=90.7367 EndY=12 EndZ=0
    g9: LineSegment StartX=90.7367 StartY=12 StartZ=0 EndX=89 EndY=9.5 EndZ=0
  constraints (26):
    c: Coincident(g0,g1)
    c: Coincident(g1,g2)
    c: Coincident(g2,g3)
    c: Coincident(g3,g0)
    c: Vertical(g0)
    c: Vertical(g2)
    c: Horizontal(g1)
    c: Horizontal(g3)
    c: Coincident(g4,g5)
    c: Coincident(g5,g6)
    c: Coincident(g6,g7)
    c: Coincident(g7,g4)
    c: Vertical(g4)
    c: Vertical(g6)
    c: Horizontal(g5)
    c: Horizontal(g7)
    c: DistanceY(g4,g4) = 5
    c: DistanceY(g0,g0) = 5
    c: Coincident(g0,g8)
    c: Coincident(g8,g9)
    c: Coincident(g9,g0)
    c: Equal(g9,g8)
    c: DistanceY(g-1,g8) = 12
    c: Symmetric(g0,g4,g-1)
    c: DistanceX(g-1,g0) = 89
    c: DistanceX(g3,g3) = 7
FEATURE [PartDesign::Pad] Pad013
  BaseFeature = -> Pocket032
  Direction = (0,0,-1)
  Length = 1.2
  Length2 = 10
  Placement = pos=(0,0,-9) rot=(1,0,0;3.14159rad)
  Profile = -> Sketch059
  ReferenceAxis = -> Sketch059 [N_Axis]
  Refine = true
  Reversed = true
  Suppressed = false
  Type = 0
FEATURE [PartDesign::Body] Body003  label="Back-panel"
  Group = -> [DatumPlane006,Sketch044,Pad010,Binder,Binder001,Binder002,Sketch046,Pad011,Sketch047,Pocket029,Sketch050,Binder003,Pad012,Sketch051,Pocket031,Sketch052,Pocket032,bumppon_A,bumppon_B,bumppon_C,bumppon_D,Sketch059,Pad013]
  Origin = -> Origin008
  Tip = -> Pad013
COMPONENT P4 — recipe-attached ("magnet", modeled in this document).
Construction recipe (the document's own serialized feature program — sketch geometry with constraints, then the solid features built on it; lengths are millimeters unless a unit is written):

FEATURE [Sketcher::SketchObject] Sketch043
  AttachmentSupport = -> [XY_Plane007]
  FullyConstrained = true
  MapMode = 5
  sketch-geometry (4):
    g0: LineSegment StartX=-2 StartY=7.5 StartZ=0 EndX=-2 EndY=-7.5 EndZ=0
    g1: LineSegment StartX=-2 StartY=-7.5 StartZ=0 EndX=2 EndY=-7.5 EndZ=0
    g2: LineSegment StartX=2 StartY=-7.5 StartZ=0 EndX=2 EndY=7.5 EndZ=0
    g3: LineSegment StartX=2 StartY=7.5 StartZ=0 EndX=-2 EndY=7.5 EndZ=0
  constraints (11):
    c: Coincident(g0,g1)
    c: Coincident(g1,g2)
    c: Coincident(g2,g3)
    c: Coincident(g3,g0)
    c: Vertical(g0)
    c: Vertical(g2)
    c: Horizontal(g1)
    c: Horizontal(g3)
    c: Symmetric(g0,g1,g-1)
    c: DistanceX(g3,g3) = 4
    c: DistanceY(g2,g2) = 15
FEATURE [PartDesign::Pad] Pad009
  Direction = (0,0,1)
  Length = 2
  Length2 = 2
  Profile = -> Sketch043
  ReferenceAxis = -> Sketch043 [N_Axis]
  Suppressed = false
  TaperAngle2 = 0.01
  Type = 4
FEATURE [PartDesign::CoordinateSystem] LCS_0003  label="frontface"
  AttacherType = Attacher::AttachEngine3D
  AttachmentSupport = -> [Pad009]
  MapMode = 45
  Placement = pos=(-1.2e-15,8e-16,-2) rot=(0,1,0;3.14159rad)
FEATURE [PartDesign::Body] magnet
  Group = -> [LCS_0003,Sketch043,Pad009]
  Origin = -> Origin007
  Tip = -> Pad009
PROVENANCE & LICENSES
A FreeCAD (.FCStd) document from a public repository crawl; recipes are the document's own serialized feature recipes (and, for linked parts, companion documents' recipes).
License: cern-ohl.
